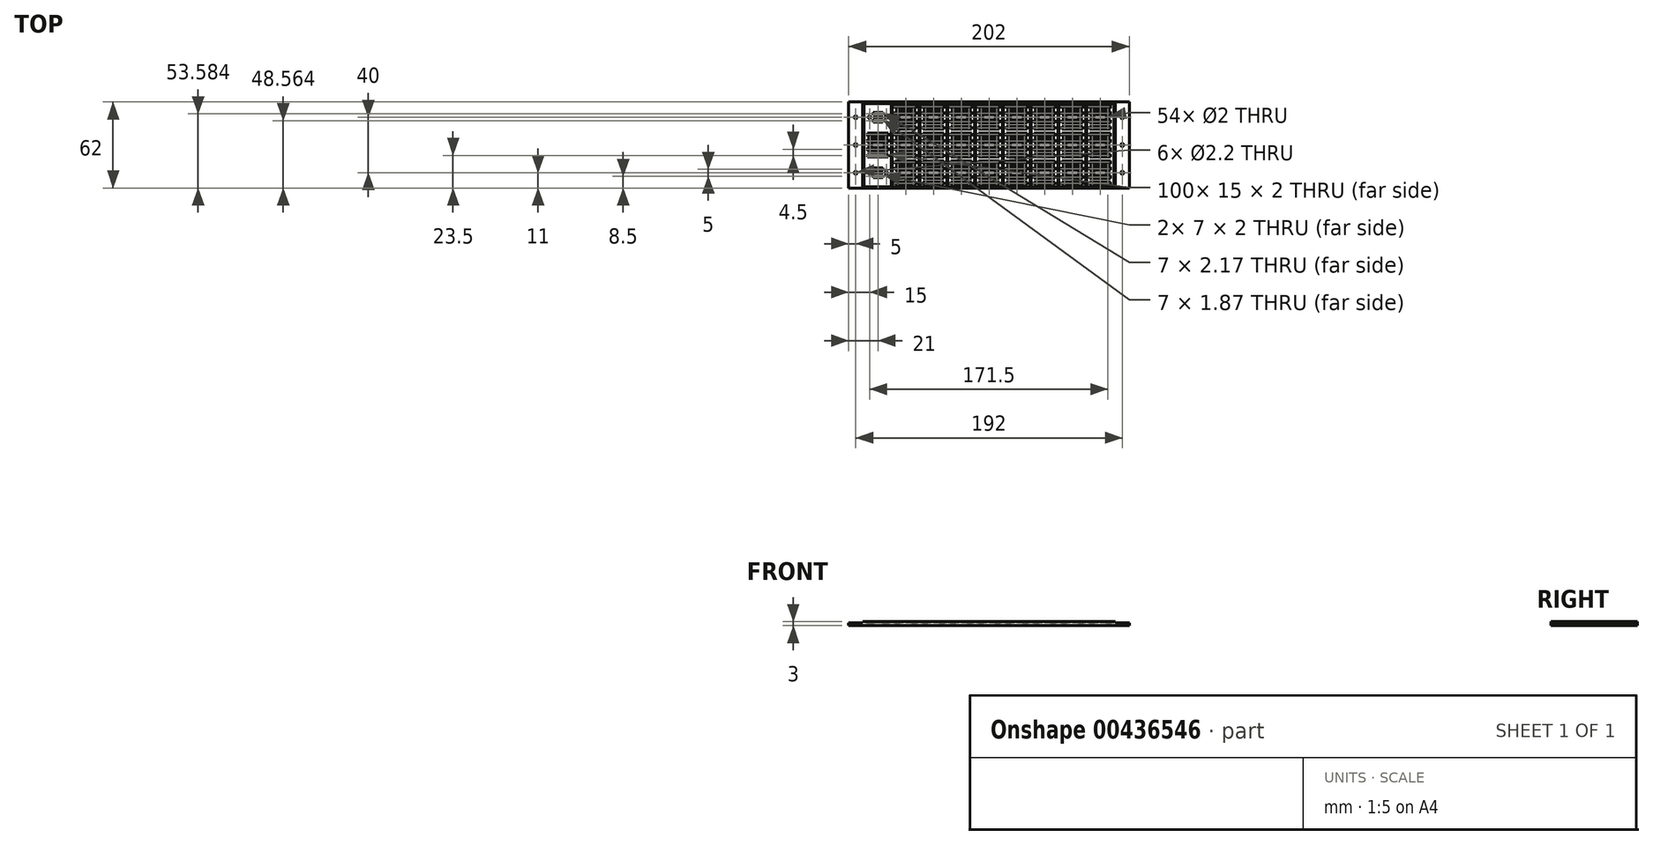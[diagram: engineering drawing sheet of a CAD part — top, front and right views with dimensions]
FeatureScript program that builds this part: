
annotation { "Feature Type Name" : "Feature", "Feature Type Description" : "" }
export const myFeature = defineFeature(function(context is Context, id is Id, definition is map)
    precondition{}
    {
        {
            var Q0;
            Q0=qCreatedBy(makeId("Top.planeOp"),FACE);
            var sketch = newSketch(context, id + "F0", { "sketchPlane" : qUnion([Q0])});
            skLineSegment(sketch, "E0.bottom", {"start": v(91, -31) * mm, "end": v(-91, -31) * mm});
            skLineSegment(sketch, "E0.top", {"start": v(91, 31) * mm, "end": v(-91, 31) * mm});
            skLineSegment(sketch, "E0.left", {"start": v(91, -31) * mm, "end": v(91, 31) * mm});
            skLineSegment(sketch, "E0.right", {"start": v(-91, -31) * mm, "end": v(-91, 31) * mm});
            skPoint(sketch, "E0.middle", {"position": v(0, 0) * mm});
            skSolve(sketch);
        }
        {
            var Q0;
            Q0=qSketchRegion(id+"F0",true);
            extrude(context, id + "F1", {"entities" : qUnion([Q0]), "depth" : 2 * mm});
        }
        {
            var Q0;
            Q0=makeQuery(id+"F1.opExtrude","CAP_FACE",FACE,{"disambiguationData":[OSD([sQuery(id+"F0.wireOp",EDGE,"E0.bottom"),sQuery(id+"F0.wireOp",EDGE,"E0.top"),sQuery(id+"F0.wireOp",EDGE,"E0.left"),sQuery(id+"F0.wireOp",EDGE,"E0.right")])],"isStart":false});
            var sketch = newSketch(context, id + "F2", { "sketchPlane" : qUnion([Q0])});
            skLineSegment(sketch, "E1.bottom", {"start": v(91, -31) * mm, "end": v(-91, -31) * mm});
            skLineSegment(sketch, "E1.top", {"start": v(91, 31) * mm, "end": v(-91, 31) * mm});
            skLineSegment(sketch, "E1.left", {"start": v(91, -31) * mm, "end": v(91, 31) * mm});
            skLineSegment(sketch, "E1.right", {"start": v(-91, -31) * mm, "end": v(-91, 31) * mm});
            skPoint(sketch, "E1.middle", {"position": v(0, 0) * mm});
            skLineSegment(sketch, "E2.bottom", {"start": v(90, -30) * mm, "end": v(-90, -30) * mm});
            skLineSegment(sketch, "E2.top", {"start": v(90, 30) * mm, "end": v(-90, 30) * mm});
            skLineSegment(sketch, "E2.left", {"start": v(90, -30) * mm, "end": v(90, 30) * mm});
            skLineSegment(sketch, "E2.right", {"start": v(-90, -30) * mm, "end": v(-90, 30) * mm});
            skSolve(sketch);
        }
        {
            var Q0;
            Q0=qSketchRegion(id+"F2",true);
            extrude(context, id + "F3", {"entities" : qUnion([Q0]), "operationType" : NewBodyOperationType.ADD, "depth" : 1 * mm});
        }
        {
            var Q0;
            Q0=qCreatedBy(makeId("Top.planeOp"),FACE);
            var sketch = newSketch(context, id + "F4", { "sketchPlane" : qUnion([Q0])});
            skLineSegment(sketch, "E3.bottom", {"start": v(-91, 31) * mm, "end": v(-101, 31) * mm});
            skLineSegment(sketch, "E3.top", {"start": v(-91, -31) * mm, "end": v(-101, -31) * mm});
            skLineSegment(sketch, "E3.left", {"start": v(-91, 31) * mm, "end": v(-91, -31) * mm});
            skLineSegment(sketch, "E3.right", {"start": v(-101, 31) * mm, "end": v(-101, -31) * mm});
            skLineSegment(sketch, "E4.bottom", {"start": v(91, 31) * mm, "end": v(101, 31) * mm});
            skLineSegment(sketch, "E4.top", {"start": v(91, -31) * mm, "end": v(101, -31) * mm});
            skLineSegment(sketch, "E4.left", {"start": v(91, 31) * mm, "end": v(91, -31) * mm});
            skLineSegment(sketch, "E4.right", {"start": v(101, 31) * mm, "end": v(101, -31) * mm});
            skCircle(sketch, "E5", {"center": v(-96, 20) * mm, "radius": 1.1 * mm});
            skPoint(sketch, "E5.centerSnap0", {"position": v(-96, 31) * mm});
            skCircle(sketch, "E6", {"center": v(-96, 0) * mm, "radius": 1.1 * mm});
            skCircle(sketch, "E7", {"center": v(-96, -20) * mm, "radius": 1.1 * mm});
            skCircle(sketch, "E8", {"center": v(96, 20) * mm, "radius": 1.1 * mm});
            skPoint(sketch, "E8.centerSnap0", {"position": v(96, 31) * mm});
            skCircle(sketch, "E9", {"center": v(96, 0) * mm, "radius": 1.1 * mm});
            skPoint(sketch, "E9.centerSnap0", {"position": v(91, 0) * mm});
            skCircle(sketch, "E10", {"center": v(96, -20) * mm, "radius": 1.1 * mm});
            skSolve(sketch);
        }
        {
            var Q0;
            Q0=qSketchRegion(id+"F4",true);
            extrude(context, id + "F5", {"entities" : qUnion([Q0]), "operationType" : NewBodyOperationType.ADD, "depth" : 2 * mm});
        }
        {
            var Q0;
            Q0=makeQuery(id+"F5.boolean.opBoolean","MERGE",FACE,{"derivedFrom":[makeQuery(id+"F1.opExtrude","CAP_FACE",FACE,{"disambiguationData":[OSD([sQuery(id+"F0.wireOp",EDGE,"E0.bottom"),sQuery(id+"F0.wireOp",EDGE,"E0.top"),sQuery(id+"F0.wireOp",EDGE,"E0.left"),sQuery(id+"F0.wireOp",EDGE,"E0.right")])],"isStart":true}),makeQuery(id+"F5.opExtrude","CAP_FACE",FACE,{"disambiguationData":[OSD([sQuery(id+"F4.wireOp",EDGE,"E3.bottom"),sQuery(id+"F4.wireOp",EDGE,"E3.top"),sQuery(id+"F4.wireOp",EDGE,"E3.left"),sQuery(id+"F4.wireOp",EDGE,"E3.right"),sQuery(id+"F4.wireOp",EDGE,"E5"),sQuery(id+"F4.wireOp",EDGE,"E6"),sQuery(id+"F4.wireOp",EDGE,"E7")])],"isStart":true}),makeQuery(id+"F5.opExtrude","CAP_FACE",FACE,{"disambiguationData":[OSD([sQuery(id+"F4.wireOp",EDGE,"E4.bottom"),sQuery(id+"F4.wireOp",EDGE,"E4.top"),sQuery(id+"F4.wireOp",EDGE,"E4.left"),sQuery(id+"F4.wireOp",EDGE,"E4.right"),sQuery(id+"F4.wireOp",EDGE,"E8"),sQuery(id+"F4.wireOp",EDGE,"E9"),sQuery(id+"F4.wireOp",EDGE,"E10")])],"isStart":true})]});
            var sketch = newSketch(context, id + "F6", { "sketchPlane" : qUnion([Q0])});
            skCircle(sketch, "E11", {"center": v(74.5, 20) * mm, "radius": 1 * mm});
            skCircle(sketch, "E12", {"center": v(85.5, 20) * mm, "radius": 1 * mm});
            skLineSegment(sketch, "E13.bottom", {"start": v(87.5, 22) * mm, "end": v(72.5, 22) * mm});
            skLineSegment(sketch, "E13.top", {"start": v(87.5, 24) * mm, "end": v(72.5, 24) * mm});
            skLineSegment(sketch, "E13.left", {"start": v(87.5, 22) * mm, "end": v(87.5, 24) * mm});
            skLineSegment(sketch, "E13.right", {"start": v(72.5, 22) * mm, "end": v(72.5, 24) * mm});
            skPoint(sketch, "E13.middle", {"position": v(80, 23) * mm});
            skLineSegment(sketch, "E14.bottom", {"start": v(87.5, 26.5) * mm, "end": v(72.5, 26.5) * mm});
            skLineSegment(sketch, "E14.top", {"start": v(87.5, 28.5) * mm, "end": v(72.5, 28.5) * mm});
            skLineSegment(sketch, "E14.left", {"start": v(87.5, 26.5) * mm, "end": v(87.5, 28.5) * mm});
            skLineSegment(sketch, "E14.right", {"start": v(72.5, 26.5) * mm, "end": v(72.5, 28.5) * mm});
            skPoint(sketch, "E14.middle", {"position": v(80, 27.5) * mm});
            skLineSegment(sketch, "E15.bottom", {"start": v(87.5, 18) * mm, "end": v(72.5, 18) * mm});
            skLineSegment(sketch, "E15.top", {"start": v(87.5, 16) * mm, "end": v(72.5, 16) * mm});
            skLineSegment(sketch, "E15.left", {"start": v(87.5, 18) * mm, "end": v(87.5, 16) * mm});
            skLineSegment(sketch, "E15.right", {"start": v(72.5, 18) * mm, "end": v(72.5, 16) * mm});
            skPoint(sketch, "E15.middle", {"position": v(80, 17) * mm});
            skLineSegment(sketch, "E16.bottom", {"start": v(87.5, 13.5) * mm, "end": v(72.5, 13.5) * mm});
            skLineSegment(sketch, "E16.top", {"start": v(87.5, 11.5) * mm, "end": v(72.5, 11.5) * mm});
            skLineSegment(sketch, "E16.left", {"start": v(87.5, 13.5) * mm, "end": v(87.5, 11.5) * mm});
            skLineSegment(sketch, "E16.right", {"start": v(72.5, 13.5) * mm, "end": v(72.5, 11.5) * mm});
            skPoint(sketch, "E16.middle", {"position": v(80, 12.5) * mm});
            skLineSegment(sketch, "E17.bottom", {"start": v(89.5, 10.5) * mm, "end": v(70.5, 10.5) * mm, "construction": true});
            skLineSegment(sketch, "E17.top", {"start": v(89.5, 29.5) * mm, "end": v(70.5, 29.5) * mm, "construction": true});
            skLineSegment(sketch, "E17.left", {"start": v(89.5, 10.5) * mm, "end": v(89.5, 29.5) * mm, "construction": true});
            skLineSegment(sketch, "E17.right", {"start": v(70.5, 10.5) * mm, "end": v(70.5, 29.5) * mm, "construction": true});
            skPoint(sketch, "E17.middle", {"position": v(80, 20) * mm});
            skLineSegment(sketch, "E18.0.1.0", {"start": v(87.5, -8.5) * mm, "end": v(72.5, -8.5) * mm});
            skLineSegment(sketch, "E18.0.1.1", {"start": v(87.5, 8.5) * mm, "end": v(72.5, 8.5) * mm});
            skLineSegment(sketch, "E18.0.1.2", {"start": v(87.5, -4) * mm, "end": v(72.5, -4) * mm});
            skLineSegment(sketch, "E18.0.1.3", {"start": v(89.5, -9.5) * mm, "end": v(70.5, -9.5) * mm, "construction": true});
            skPoint(sketch, "E18.0.1.4", {"position": v(80, -3) * mm});
            skLineSegment(sketch, "E18.0.1.5", {"start": v(89.5, 9.5) * mm, "end": v(70.5, 9.5) * mm, "construction": true});
            skLineSegment(sketch, "E18.0.1.6", {"start": v(87.5, 6.5) * mm, "end": v(72.5, 6.5) * mm});
            skLineSegment(sketch, "E18.0.1.7", {"start": v(89.5, -9.5) * mm, "end": v(89.5, 9.5) * mm, "construction": true});
            skPoint(sketch, "E18.0.1.8", {"position": v(80, 3) * mm});
            skLineSegment(sketch, "E18.0.1.9", {"start": v(87.5, -6.5) * mm, "end": v(72.5, -6.5) * mm});
            skLineSegment(sketch, "E18.0.1.10", {"start": v(87.5, 4) * mm, "end": v(72.5, 4) * mm});
            skLineSegment(sketch, "E18.0.1.11", {"start": v(87.5, -2) * mm, "end": v(72.5, -2) * mm});
            skPoint(sketch, "E18.0.1.12", {"position": v(80, 7.5) * mm});
            skLineSegment(sketch, "E18.0.1.13", {"start": v(70.5, -9.5) * mm, "end": v(70.5, 9.5) * mm, "construction": true});
            skPoint(sketch, "E18.0.1.14", {"position": v(80, -7.5) * mm});
            skLineSegment(sketch, "E18.0.1.15", {"start": v(87.5, 2) * mm, "end": v(72.5, 2) * mm});
            skCircle(sketch, "E18.0.1.16", {"center": v(74.5, 0) * mm, "radius": 1 * mm});
            skCircle(sketch, "E18.0.1.17", {"center": v(85.5, 0) * mm, "radius": 1 * mm});
            skPoint(sketch, "E18.0.1.18", {"position": v(80, 0) * mm});
            skLineSegment(sketch, "E18.0.1.19", {"start": v(72.5, -6.5) * mm, "end": v(72.5, -8.5) * mm});
            skLineSegment(sketch, "E18.0.1.20", {"start": v(87.5, 6.5) * mm, "end": v(87.5, 8.5) * mm});
            skLineSegment(sketch, "E18.0.1.21", {"start": v(72.5, 6.5) * mm, "end": v(72.5, 8.5) * mm});
            skLineSegment(sketch, "E18.0.1.22", {"start": v(87.5, -2) * mm, "end": v(87.5, -4) * mm});
            skLineSegment(sketch, "E18.0.1.23", {"start": v(87.5, 2) * mm, "end": v(87.5, 4) * mm});
            skLineSegment(sketch, "E18.0.1.24", {"start": v(72.5, 2) * mm, "end": v(72.5, 4) * mm});
            skLineSegment(sketch, "E18.0.1.25", {"start": v(87.5, -6.5) * mm, "end": v(87.5, -8.5) * mm});
            skLineSegment(sketch, "E18.0.1.26", {"start": v(72.5, -2) * mm, "end": v(72.5, -4) * mm});
            skLineSegment(sketch, "E18.0.2.0", {"start": v(87.5, -28.5) * mm, "end": v(72.5, -28.5) * mm});
            skLineSegment(sketch, "E18.0.2.1", {"start": v(87.5, -11.5) * mm, "end": v(72.5, -11.5) * mm});
            skLineSegment(sketch, "E18.0.2.2", {"start": v(87.5, -24) * mm, "end": v(72.5, -24) * mm});
            skLineSegment(sketch, "E18.0.2.3", {"start": v(89.5, -29.5) * mm, "end": v(70.5, -29.5) * mm, "construction": true});
            skPoint(sketch, "E18.0.2.4", {"position": v(80, -23) * mm});
            skLineSegment(sketch, "E18.0.2.5", {"start": v(89.5, -10.5) * mm, "end": v(70.5, -10.5) * mm, "construction": true});
            skLineSegment(sketch, "E18.0.2.6", {"start": v(87.5, -13.5) * mm, "end": v(72.5, -13.5) * mm});
            skLineSegment(sketch, "E18.0.2.7", {"start": v(89.5, -29.5) * mm, "end": v(89.5, -10.5) * mm, "construction": true});
            skPoint(sketch, "E18.0.2.8", {"position": v(80, -17) * mm});
            skLineSegment(sketch, "E18.0.2.9", {"start": v(87.5, -26.5) * mm, "end": v(72.5, -26.5) * mm});
            skLineSegment(sketch, "E18.0.2.10", {"start": v(87.5, -16) * mm, "end": v(72.5, -16) * mm});
            skLineSegment(sketch, "E18.0.2.11", {"start": v(87.5, -22) * mm, "end": v(72.5, -22) * mm});
            skPoint(sketch, "E18.0.2.12", {"position": v(80, -12.5) * mm});
            skLineSegment(sketch, "E18.0.2.13", {"start": v(70.5, -29.5) * mm, "end": v(70.5, -10.5) * mm, "construction": true});
            skPoint(sketch, "E18.0.2.14", {"position": v(80, -27.5) * mm});
            skLineSegment(sketch, "E18.0.2.15", {"start": v(87.5, -18) * mm, "end": v(72.5, -18) * mm});
            skCircle(sketch, "E18.0.2.16", {"center": v(74.5, -20) * mm, "radius": 1 * mm});
            skCircle(sketch, "E18.0.2.17", {"center": v(85.5, -20) * mm, "radius": 1 * mm});
            skPoint(sketch, "E18.0.2.18", {"position": v(80, -20) * mm});
            skLineSegment(sketch, "E18.0.2.19", {"start": v(72.5, -26.5) * mm, "end": v(72.5, -28.5) * mm});
            skLineSegment(sketch, "E18.0.2.20", {"start": v(87.5, -13.5) * mm, "end": v(87.5, -11.5) * mm});
            skLineSegment(sketch, "E18.0.2.21", {"start": v(72.5, -13.5) * mm, "end": v(72.5, -11.5) * mm});
            skLineSegment(sketch, "E18.0.2.22", {"start": v(87.5, -22) * mm, "end": v(87.5, -24) * mm});
            skLineSegment(sketch, "E18.0.2.23", {"start": v(87.5, -18) * mm, "end": v(87.5, -16) * mm});
            skLineSegment(sketch, "E18.0.2.24", {"start": v(72.5, -18) * mm, "end": v(72.5, -16) * mm});
            skLineSegment(sketch, "E18.0.2.25", {"start": v(87.5, -26.5) * mm, "end": v(87.5, -28.5) * mm});
            skLineSegment(sketch, "E18.0.2.26", {"start": v(72.5, -22) * mm, "end": v(72.5, -24) * mm});
            skLineSegment(sketch, "E18.1.0.0", {"start": v(67.5, 11.5) * mm, "end": v(52.5, 11.5) * mm});
            skLineSegment(sketch, "E18.1.0.1", {"start": v(67.5, 28.5) * mm, "end": v(52.5, 28.5) * mm});
            skLineSegment(sketch, "E18.1.0.2", {"start": v(67.5, 16) * mm, "end": v(52.5, 16) * mm});
            skLineSegment(sketch, "E18.1.0.3", {"start": v(69.5, 10.5) * mm, "end": v(50.5, 10.5) * mm, "construction": true});
            skPoint(sketch, "E18.1.0.4", {"position": v(60, 17) * mm});
            skLineSegment(sketch, "E18.1.0.5", {"start": v(69.5, 29.5) * mm, "end": v(50.5, 29.5) * mm, "construction": true});
            skLineSegment(sketch, "E18.1.0.6", {"start": v(67.5, 26.5) * mm, "end": v(52.5, 26.5) * mm});
            skLineSegment(sketch, "E18.1.0.7", {"start": v(69.5, 10.5) * mm, "end": v(69.5, 29.5) * mm, "construction": true});
            skPoint(sketch, "E18.1.0.8", {"position": v(60, 23) * mm});
            skLineSegment(sketch, "E18.1.0.9", {"start": v(67.5, 13.5) * mm, "end": v(52.5, 13.5) * mm});
            skLineSegment(sketch, "E18.1.0.10", {"start": v(67.5, 24) * mm, "end": v(52.5, 24) * mm});
            skLineSegment(sketch, "E18.1.0.11", {"start": v(67.5, 18) * mm, "end": v(52.5, 18) * mm});
            skPoint(sketch, "E18.1.0.12", {"position": v(60, 27.5) * mm});
            skLineSegment(sketch, "E18.1.0.13", {"start": v(50.5, 10.5) * mm, "end": v(50.5, 29.5) * mm, "construction": true});
            skPoint(sketch, "E18.1.0.14", {"position": v(60, 12.5) * mm});
            skLineSegment(sketch, "E18.1.0.15", {"start": v(67.5, 22) * mm, "end": v(52.5, 22) * mm});
            skCircle(sketch, "E18.1.0.16", {"center": v(54.5, 20) * mm, "radius": 1 * mm});
            skCircle(sketch, "E18.1.0.17", {"center": v(65.5, 20) * mm, "radius": 1 * mm});
            skPoint(sketch, "E18.1.0.18", {"position": v(60, 20) * mm});
            skLineSegment(sketch, "E18.1.0.19", {"start": v(52.5, 13.5) * mm, "end": v(52.5, 11.5) * mm});
            skLineSegment(sketch, "E18.1.0.20", {"start": v(67.5, 26.5) * mm, "end": v(67.5, 28.5) * mm});
            skLineSegment(sketch, "E18.1.0.21", {"start": v(52.5, 26.5) * mm, "end": v(52.5, 28.5) * mm});
            skLineSegment(sketch, "E18.1.0.22", {"start": v(67.5, 18) * mm, "end": v(67.5, 16) * mm});
            skLineSegment(sketch, "E18.1.0.23", {"start": v(67.5, 22) * mm, "end": v(67.5, 24) * mm});
            skLineSegment(sketch, "E18.1.0.24", {"start": v(52.5, 22) * mm, "end": v(52.5, 24) * mm});
            skLineSegment(sketch, "E18.1.0.25", {"start": v(67.5, 13.5) * mm, "end": v(67.5, 11.5) * mm});
            skLineSegment(sketch, "E18.1.0.26", {"start": v(52.5, 18) * mm, "end": v(52.5, 16) * mm});
            skLineSegment(sketch, "E18.1.1.0", {"start": v(67.5, -8.5) * mm, "end": v(52.5, -8.5) * mm});
            skLineSegment(sketch, "E18.1.1.1", {"start": v(67.5, 8.5) * mm, "end": v(52.5, 8.5) * mm});
            skLineSegment(sketch, "E18.1.1.2", {"start": v(67.5, -4) * mm, "end": v(52.5, -4) * mm});
            skLineSegment(sketch, "E18.1.1.3", {"start": v(69.5, -9.5) * mm, "end": v(50.5, -9.5) * mm, "construction": true});
            skPoint(sketch, "E18.1.1.4", {"position": v(60, -3) * mm});
            skLineSegment(sketch, "E18.1.1.5", {"start": v(69.5, 9.5) * mm, "end": v(50.5, 9.5) * mm, "construction": true});
            skLineSegment(sketch, "E18.1.1.6", {"start": v(67.5, 6.5) * mm, "end": v(52.5, 6.5) * mm});
            skLineSegment(sketch, "E18.1.1.7", {"start": v(69.5, -9.5) * mm, "end": v(69.5, 9.5) * mm, "construction": true});
            skPoint(sketch, "E18.1.1.8", {"position": v(60, 3) * mm});
            skLineSegment(sketch, "E18.1.1.9", {"start": v(67.5, -6.5) * mm, "end": v(52.5, -6.5) * mm});
            skLineSegment(sketch, "E18.1.1.10", {"start": v(67.5, 4) * mm, "end": v(52.5, 4) * mm});
            skLineSegment(sketch, "E18.1.1.11", {"start": v(67.5, -2) * mm, "end": v(52.5, -2) * mm});
            skPoint(sketch, "E18.1.1.12", {"position": v(60, 7.5) * mm});
            skLineSegment(sketch, "E18.1.1.13", {"start": v(50.5, -9.5) * mm, "end": v(50.5, 9.5) * mm, "construction": true});
            skPoint(sketch, "E18.1.1.14", {"position": v(60, -7.5) * mm});
            skLineSegment(sketch, "E18.1.1.15", {"start": v(67.5, 2) * mm, "end": v(52.5, 2) * mm});
            skCircle(sketch, "E18.1.1.16", {"center": v(54.5, 0) * mm, "radius": 1 * mm});
            skCircle(sketch, "E18.1.1.17", {"center": v(65.5, 0) * mm, "radius": 1 * mm});
            skPoint(sketch, "E18.1.1.18", {"position": v(60, 0) * mm});
            skLineSegment(sketch, "E18.1.1.19", {"start": v(52.5, -6.5) * mm, "end": v(52.5, -8.5) * mm});
            skLineSegment(sketch, "E18.1.1.20", {"start": v(67.5, 6.5) * mm, "end": v(67.5, 8.5) * mm});
            skLineSegment(sketch, "E18.1.1.21", {"start": v(52.5, 6.5) * mm, "end": v(52.5, 8.5) * mm});
            skLineSegment(sketch, "E18.1.1.22", {"start": v(67.5, -2) * mm, "end": v(67.5, -4) * mm});
            skLineSegment(sketch, "E18.1.1.23", {"start": v(67.5, 2) * mm, "end": v(67.5, 4) * mm});
            skLineSegment(sketch, "E18.1.1.24", {"start": v(52.5, 2) * mm, "end": v(52.5, 4) * mm});
            skLineSegment(sketch, "E18.1.1.25", {"start": v(67.5, -6.5) * mm, "end": v(67.5, -8.5) * mm});
            skLineSegment(sketch, "E18.1.1.26", {"start": v(52.5, -2) * mm, "end": v(52.5, -4) * mm});
            skLineSegment(sketch, "E18.1.2.0", {"start": v(67.5, -28.5) * mm, "end": v(52.5, -28.5) * mm});
            skLineSegment(sketch, "E18.1.2.1", {"start": v(67.5, -11.5) * mm, "end": v(52.5, -11.5) * mm});
            skLineSegment(sketch, "E18.1.2.2", {"start": v(67.5, -24) * mm, "end": v(52.5, -24) * mm});
            skLineSegment(sketch, "E18.1.2.3", {"start": v(69.5, -29.5) * mm, "end": v(50.5, -29.5) * mm, "construction": true});
            skPoint(sketch, "E18.1.2.4", {"position": v(60, -23) * mm});
            skLineSegment(sketch, "E18.1.2.5", {"start": v(69.5, -10.5) * mm, "end": v(50.5, -10.5) * mm, "construction": true});
            skLineSegment(sketch, "E18.1.2.6", {"start": v(67.5, -13.5) * mm, "end": v(52.5, -13.5) * mm});
            skLineSegment(sketch, "E18.1.2.7", {"start": v(69.5, -29.5) * mm, "end": v(69.5, -10.5) * mm, "construction": true});
            skPoint(sketch, "E18.1.2.8", {"position": v(60, -17) * mm});
            skLineSegment(sketch, "E18.1.2.9", {"start": v(67.5, -26.5) * mm, "end": v(52.5, -26.5) * mm});
            skLineSegment(sketch, "E18.1.2.10", {"start": v(67.5, -16) * mm, "end": v(52.5, -16) * mm});
            skLineSegment(sketch, "E18.1.2.11", {"start": v(67.5, -22) * mm, "end": v(52.5, -22) * mm});
            skPoint(sketch, "E18.1.2.12", {"position": v(60, -12.5) * mm});
            skLineSegment(sketch, "E18.1.2.13", {"start": v(50.5, -29.5) * mm, "end": v(50.5, -10.5) * mm, "construction": true});
            skPoint(sketch, "E18.1.2.14", {"position": v(60, -27.5) * mm});
            skLineSegment(sketch, "E18.1.2.15", {"start": v(67.5, -18) * mm, "end": v(52.5, -18) * mm});
            skCircle(sketch, "E18.1.2.16", {"center": v(54.5, -20) * mm, "radius": 1 * mm});
            skCircle(sketch, "E18.1.2.17", {"center": v(65.5, -20) * mm, "radius": 1 * mm});
            skPoint(sketch, "E18.1.2.18", {"position": v(60, -20) * mm});
            skLineSegment(sketch, "E18.1.2.19", {"start": v(52.5, -26.5) * mm, "end": v(52.5, -28.5) * mm});
            skLineSegment(sketch, "E18.1.2.20", {"start": v(67.5, -13.5) * mm, "end": v(67.5, -11.5) * mm});
            skLineSegment(sketch, "E18.1.2.21", {"start": v(52.5, -13.5) * mm, "end": v(52.5, -11.5) * mm});
            skLineSegment(sketch, "E18.1.2.22", {"start": v(67.5, -22) * mm, "end": v(67.5, -24) * mm});
            skLineSegment(sketch, "E18.1.2.23", {"start": v(67.5, -18) * mm, "end": v(67.5, -16) * mm});
            skLineSegment(sketch, "E18.1.2.24", {"start": v(52.5, -18) * mm, "end": v(52.5, -16) * mm});
            skLineSegment(sketch, "E18.1.2.25", {"start": v(67.5, -26.5) * mm, "end": v(67.5, -28.5) * mm});
            skLineSegment(sketch, "E18.1.2.26", {"start": v(52.5, -22) * mm, "end": v(52.5, -24) * mm});
            skLineSegment(sketch, "E18.2.0.0", {"start": v(47.5, 11.5) * mm, "end": v(32.5, 11.5) * mm});
            skLineSegment(sketch, "E18.2.0.1", {"start": v(47.5, 28.5) * mm, "end": v(32.5, 28.5) * mm});
            skLineSegment(sketch, "E18.2.0.2", {"start": v(47.5, 16) * mm, "end": v(32.5, 16) * mm});
            skLineSegment(sketch, "E18.2.0.3", {"start": v(49.5, 10.5) * mm, "end": v(30.5, 10.5) * mm, "construction": true});
            skPoint(sketch, "E18.2.0.4", {"position": v(40, 17) * mm});
            skLineSegment(sketch, "E18.2.0.5", {"start": v(49.5, 29.5) * mm, "end": v(30.5, 29.5) * mm, "construction": true});
            skLineSegment(sketch, "E18.2.0.6", {"start": v(47.5, 26.5) * mm, "end": v(32.5, 26.5) * mm});
            skLineSegment(sketch, "E18.2.0.7", {"start": v(49.5, 10.5) * mm, "end": v(49.5, 29.5) * mm, "construction": true});
            skPoint(sketch, "E18.2.0.8", {"position": v(40, 23) * mm});
            skLineSegment(sketch, "E18.2.0.9", {"start": v(47.5, 13.5) * mm, "end": v(32.5, 13.5) * mm});
            skLineSegment(sketch, "E18.2.0.10", {"start": v(47.5, 24) * mm, "end": v(32.5, 24) * mm});
            skLineSegment(sketch, "E18.2.0.11", {"start": v(47.5, 18) * mm, "end": v(32.5, 18) * mm});
            skPoint(sketch, "E18.2.0.12", {"position": v(40, 27.5) * mm});
            skLineSegment(sketch, "E18.2.0.13", {"start": v(30.5, 10.5) * mm, "end": v(30.5, 29.5) * mm, "construction": true});
            skPoint(sketch, "E18.2.0.14", {"position": v(40, 12.5) * mm});
            skLineSegment(sketch, "E18.2.0.15", {"start": v(47.5, 22) * mm, "end": v(32.5, 22) * mm});
            skCircle(sketch, "E18.2.0.16", {"center": v(34.5, 20) * mm, "radius": 1 * mm});
            skCircle(sketch, "E18.2.0.17", {"center": v(45.5, 20) * mm, "radius": 1 * mm});
            skPoint(sketch, "E18.2.0.18", {"position": v(40, 20) * mm});
            skLineSegment(sketch, "E18.2.0.19", {"start": v(32.5, 13.5) * mm, "end": v(32.5, 11.5) * mm});
            skLineSegment(sketch, "E18.2.0.20", {"start": v(47.5, 26.5) * mm, "end": v(47.5, 28.5) * mm});
            skLineSegment(sketch, "E18.2.0.21", {"start": v(32.5, 26.5) * mm, "end": v(32.5, 28.5) * mm});
            skLineSegment(sketch, "E18.2.0.22", {"start": v(47.5, 18) * mm, "end": v(47.5, 16) * mm});
            skLineSegment(sketch, "E18.2.0.23", {"start": v(47.5, 22) * mm, "end": v(47.5, 24) * mm});
            skLineSegment(sketch, "E18.2.0.24", {"start": v(32.5, 22) * mm, "end": v(32.5, 24) * mm});
            skLineSegment(sketch, "E18.2.0.25", {"start": v(47.5, 13.5) * mm, "end": v(47.5, 11.5) * mm});
            skLineSegment(sketch, "E18.2.0.26", {"start": v(32.5, 18) * mm, "end": v(32.5, 16) * mm});
            skLineSegment(sketch, "E18.2.1.0", {"start": v(47.5, -8.5) * mm, "end": v(32.5, -8.5) * mm});
            skLineSegment(sketch, "E18.2.1.1", {"start": v(47.5, 8.5) * mm, "end": v(32.5, 8.5) * mm});
            skLineSegment(sketch, "E18.2.1.2", {"start": v(47.5, -4) * mm, "end": v(32.5, -4) * mm});
            skLineSegment(sketch, "E18.2.1.3", {"start": v(49.5, -9.5) * mm, "end": v(30.5, -9.5) * mm, "construction": true});
            skPoint(sketch, "E18.2.1.4", {"position": v(40, -3) * mm});
            skLineSegment(sketch, "E18.2.1.5", {"start": v(49.5, 9.5) * mm, "end": v(30.5, 9.5) * mm, "construction": true});
            skLineSegment(sketch, "E18.2.1.6", {"start": v(47.5, 6.5) * mm, "end": v(32.5, 6.5) * mm});
            skLineSegment(sketch, "E18.2.1.7", {"start": v(49.5, -9.5) * mm, "end": v(49.5, 9.5) * mm, "construction": true});
            skPoint(sketch, "E18.2.1.8", {"position": v(40, 3) * mm});
            skLineSegment(sketch, "E18.2.1.9", {"start": v(47.5, -6.5) * mm, "end": v(32.5, -6.5) * mm});
            skLineSegment(sketch, "E18.2.1.10", {"start": v(47.5, 4) * mm, "end": v(32.5, 4) * mm});
            skLineSegment(sketch, "E18.2.1.11", {"start": v(47.5, -2) * mm, "end": v(32.5, -2) * mm});
            skPoint(sketch, "E18.2.1.12", {"position": v(40, 7.5) * mm});
            skLineSegment(sketch, "E18.2.1.13", {"start": v(30.5, -9.5) * mm, "end": v(30.5, 9.5) * mm, "construction": true});
            skPoint(sketch, "E18.2.1.14", {"position": v(40, -7.5) * mm});
            skLineSegment(sketch, "E18.2.1.15", {"start": v(47.5, 2) * mm, "end": v(32.5, 2) * mm});
            skCircle(sketch, "E18.2.1.16", {"center": v(34.5, 0) * mm, "radius": 1 * mm});
            skCircle(sketch, "E18.2.1.17", {"center": v(45.5, 0) * mm, "radius": 1 * mm});
            skPoint(sketch, "E18.2.1.18", {"position": v(40, 0) * mm});
            skLineSegment(sketch, "E18.2.1.19", {"start": v(32.5, -6.5) * mm, "end": v(32.5, -8.5) * mm});
            skLineSegment(sketch, "E18.2.1.20", {"start": v(47.5, 6.5) * mm, "end": v(47.5, 8.5) * mm});
            skLineSegment(sketch, "E18.2.1.21", {"start": v(32.5, 6.5) * mm, "end": v(32.5, 8.5) * mm});
            skLineSegment(sketch, "E18.2.1.22", {"start": v(47.5, -2) * mm, "end": v(47.5, -4) * mm});
            skLineSegment(sketch, "E18.2.1.23", {"start": v(47.5, 2) * mm, "end": v(47.5, 4) * mm});
            skLineSegment(sketch, "E18.2.1.24", {"start": v(32.5, 2) * mm, "end": v(32.5, 4) * mm});
            skLineSegment(sketch, "E18.2.1.25", {"start": v(47.5, -6.5) * mm, "end": v(47.5, -8.5) * mm});
            skLineSegment(sketch, "E18.2.1.26", {"start": v(32.5, -2) * mm, "end": v(32.5, -4) * mm});
            skLineSegment(sketch, "E18.2.2.0", {"start": v(47.5, -28.5) * mm, "end": v(32.5, -28.5) * mm});
            skLineSegment(sketch, "E18.2.2.1", {"start": v(47.5, -11.5) * mm, "end": v(32.5, -11.5) * mm});
            skLineSegment(sketch, "E18.2.2.2", {"start": v(47.5, -24) * mm, "end": v(32.5, -24) * mm});
            skLineSegment(sketch, "E18.2.2.3", {"start": v(49.5, -29.5) * mm, "end": v(30.5, -29.5) * mm, "construction": true});
            skPoint(sketch, "E18.2.2.4", {"position": v(40, -23) * mm});
            skLineSegment(sketch, "E18.2.2.5", {"start": v(49.5, -10.5) * mm, "end": v(30.5, -10.5) * mm, "construction": true});
            skLineSegment(sketch, "E18.2.2.6", {"start": v(47.5, -13.5) * mm, "end": v(32.5, -13.5) * mm});
            skLineSegment(sketch, "E18.2.2.7", {"start": v(49.5, -29.5) * mm, "end": v(49.5, -10.5) * mm, "construction": true});
            skPoint(sketch, "E18.2.2.8", {"position": v(40, -17) * mm});
            skLineSegment(sketch, "E18.2.2.9", {"start": v(47.5, -26.5) * mm, "end": v(32.5, -26.5) * mm});
            skLineSegment(sketch, "E18.2.2.10", {"start": v(47.5, -16) * mm, "end": v(32.5, -16) * mm});
            skLineSegment(sketch, "E18.2.2.11", {"start": v(47.5, -22) * mm, "end": v(32.5, -22) * mm});
            skPoint(sketch, "E18.2.2.12", {"position": v(40, -12.5) * mm});
            skLineSegment(sketch, "E18.2.2.13", {"start": v(30.5, -29.5) * mm, "end": v(30.5, -10.5) * mm, "construction": true});
            skPoint(sketch, "E18.2.2.14", {"position": v(40, -27.5) * mm});
            skLineSegment(sketch, "E18.2.2.15", {"start": v(47.5, -18) * mm, "end": v(32.5, -18) * mm});
            skCircle(sketch, "E18.2.2.16", {"center": v(34.5, -20) * mm, "radius": 1 * mm});
            skCircle(sketch, "E18.2.2.17", {"center": v(45.5, -20) * mm, "radius": 1 * mm});
            skPoint(sketch, "E18.2.2.18", {"position": v(40, -20) * mm});
            skLineSegment(sketch, "E18.2.2.19", {"start": v(32.5, -26.5) * mm, "end": v(32.5, -28.5) * mm});
            skLineSegment(sketch, "E18.2.2.20", {"start": v(47.5, -13.5) * mm, "end": v(47.5, -11.5) * mm});
            skLineSegment(sketch, "E18.2.2.21", {"start": v(32.5, -13.5) * mm, "end": v(32.5, -11.5) * mm});
            skLineSegment(sketch, "E18.2.2.22", {"start": v(47.5, -22) * mm, "end": v(47.5, -24) * mm});
            skLineSegment(sketch, "E18.2.2.23", {"start": v(47.5, -18) * mm, "end": v(47.5, -16) * mm});
            skLineSegment(sketch, "E18.2.2.24", {"start": v(32.5, -18) * mm, "end": v(32.5, -16) * mm});
            skLineSegment(sketch, "E18.2.2.25", {"start": v(47.5, -26.5) * mm, "end": v(47.5, -28.5) * mm});
            skLineSegment(sketch, "E18.2.2.26", {"start": v(32.5, -22) * mm, "end": v(32.5, -24) * mm});
            skLineSegment(sketch, "E18.3.0.0", {"start": v(27.5, 11.5) * mm, "end": v(12.5, 11.5) * mm});
            skLineSegment(sketch, "E18.3.0.1", {"start": v(27.5, 28.5) * mm, "end": v(12.5, 28.5) * mm});
            skLineSegment(sketch, "E18.3.0.2", {"start": v(27.5, 16) * mm, "end": v(12.5, 16) * mm});
            skLineSegment(sketch, "E18.3.0.3", {"start": v(29.5, 10.5) * mm, "end": v(10.5, 10.5) * mm, "construction": true});
            skPoint(sketch, "E18.3.0.4", {"position": v(20, 17) * mm});
            skLineSegment(sketch, "E18.3.0.5", {"start": v(29.5, 29.5) * mm, "end": v(10.5, 29.5) * mm, "construction": true});
            skLineSegment(sketch, "E18.3.0.6", {"start": v(27.5, 26.5) * mm, "end": v(12.5, 26.5) * mm});
            skLineSegment(sketch, "E18.3.0.7", {"start": v(29.5, 10.5) * mm, "end": v(29.5, 29.5) * mm, "construction": true});
            skPoint(sketch, "E18.3.0.8", {"position": v(20, 23) * mm});
            skLineSegment(sketch, "E18.3.0.9", {"start": v(27.5, 13.5) * mm, "end": v(12.5, 13.5) * mm});
            skLineSegment(sketch, "E18.3.0.10", {"start": v(27.5, 24) * mm, "end": v(12.5, 24) * mm});
            skLineSegment(sketch, "E18.3.0.11", {"start": v(27.5, 18) * mm, "end": v(12.5, 18) * mm});
            skPoint(sketch, "E18.3.0.12", {"position": v(20, 27.5) * mm});
            skLineSegment(sketch, "E18.3.0.13", {"start": v(10.5, 10.5) * mm, "end": v(10.5, 29.5) * mm, "construction": true});
            skPoint(sketch, "E18.3.0.14", {"position": v(20, 12.5) * mm});
            skLineSegment(sketch, "E18.3.0.15", {"start": v(27.5, 22) * mm, "end": v(12.5, 22) * mm});
            skCircle(sketch, "E18.3.0.16", {"center": v(14.5, 20) * mm, "radius": 1 * mm});
            skCircle(sketch, "E18.3.0.17", {"center": v(25.5, 20) * mm, "radius": 1 * mm});
            skPoint(sketch, "E18.3.0.18", {"position": v(20, 20) * mm});
            skLineSegment(sketch, "E18.3.0.19", {"start": v(12.5, 13.5) * mm, "end": v(12.5, 11.5) * mm});
            skLineSegment(sketch, "E18.3.0.20", {"start": v(27.5, 26.5) * mm, "end": v(27.5, 28.5) * mm});
            skLineSegment(sketch, "E18.3.0.21", {"start": v(12.5, 26.5) * mm, "end": v(12.5, 28.5) * mm});
            skLineSegment(sketch, "E18.3.0.22", {"start": v(27.5, 18) * mm, "end": v(27.5, 16) * mm});
            skLineSegment(sketch, "E18.3.0.23", {"start": v(27.5, 22) * mm, "end": v(27.5, 24) * mm});
            skLineSegment(sketch, "E18.3.0.24", {"start": v(12.5, 22) * mm, "end": v(12.5, 24) * mm});
            skLineSegment(sketch, "E18.3.0.25", {"start": v(27.5, 13.5) * mm, "end": v(27.5, 11.5) * mm});
            skLineSegment(sketch, "E18.3.0.26", {"start": v(12.5, 18) * mm, "end": v(12.5, 16) * mm});
            skLineSegment(sketch, "E18.3.1.0", {"start": v(27.5, -8.5) * mm, "end": v(12.5, -8.5) * mm});
            skLineSegment(sketch, "E18.3.1.1", {"start": v(27.5, 8.5) * mm, "end": v(12.5, 8.5) * mm});
            skLineSegment(sketch, "E18.3.1.2", {"start": v(27.5, -4) * mm, "end": v(12.5, -4) * mm});
            skLineSegment(sketch, "E18.3.1.3", {"start": v(29.5, -9.5) * mm, "end": v(10.5, -9.5) * mm, "construction": true});
            skPoint(sketch, "E18.3.1.4", {"position": v(20, -3) * mm});
            skLineSegment(sketch, "E18.3.1.5", {"start": v(29.5, 9.5) * mm, "end": v(10.5, 9.5) * mm, "construction": true});
            skLineSegment(sketch, "E18.3.1.6", {"start": v(27.5, 6.5) * mm, "end": v(12.5, 6.5) * mm});
            skLineSegment(sketch, "E18.3.1.7", {"start": v(29.5, -9.5) * mm, "end": v(29.5, 9.5) * mm, "construction": true});
            skPoint(sketch, "E18.3.1.8", {"position": v(20, 3) * mm});
            skLineSegment(sketch, "E18.3.1.9", {"start": v(27.5, -6.5) * mm, "end": v(12.5, -6.5) * mm});
            skLineSegment(sketch, "E18.3.1.10", {"start": v(27.5, 4) * mm, "end": v(12.5, 4) * mm});
            skLineSegment(sketch, "E18.3.1.11", {"start": v(27.5, -2) * mm, "end": v(12.5, -2) * mm});
            skPoint(sketch, "E18.3.1.12", {"position": v(20, 7.5) * mm});
            skLineSegment(sketch, "E18.3.1.13", {"start": v(10.5, -9.5) * mm, "end": v(10.5, 9.5) * mm, "construction": true});
            skPoint(sketch, "E18.3.1.14", {"position": v(20, -7.5) * mm});
            skLineSegment(sketch, "E18.3.1.15", {"start": v(27.5, 2) * mm, "end": v(12.5, 2) * mm});
            skCircle(sketch, "E18.3.1.16", {"center": v(14.5, 0) * mm, "radius": 1 * mm});
            skCircle(sketch, "E18.3.1.17", {"center": v(25.5, 0) * mm, "radius": 1 * mm});
            skPoint(sketch, "E18.3.1.18", {"position": v(20, 0) * mm});
            skLineSegment(sketch, "E18.3.1.19", {"start": v(12.5, -6.5) * mm, "end": v(12.5, -8.5) * mm});
            skLineSegment(sketch, "E18.3.1.20", {"start": v(27.5, 6.5) * mm, "end": v(27.5, 8.5) * mm});
            skLineSegment(sketch, "E18.3.1.21", {"start": v(12.5, 6.5) * mm, "end": v(12.5, 8.5) * mm});
            skLineSegment(sketch, "E18.3.1.22", {"start": v(27.5, -2) * mm, "end": v(27.5, -4) * mm});
            skLineSegment(sketch, "E18.3.1.23", {"start": v(27.5, 2) * mm, "end": v(27.5, 4) * mm});
            skLineSegment(sketch, "E18.3.1.24", {"start": v(12.5, 2) * mm, "end": v(12.5, 4) * mm});
            skLineSegment(sketch, "E18.3.1.25", {"start": v(27.5, -6.5) * mm, "end": v(27.5, -8.5) * mm});
            skLineSegment(sketch, "E18.3.1.26", {"start": v(12.5, -2) * mm, "end": v(12.5, -4) * mm});
            skLineSegment(sketch, "E18.3.2.0", {"start": v(27.5, -28.5) * mm, "end": v(12.5, -28.5) * mm});
            skLineSegment(sketch, "E18.3.2.1", {"start": v(27.5, -11.5) * mm, "end": v(12.5, -11.5) * mm});
            skLineSegment(sketch, "E18.3.2.2", {"start": v(27.5, -24) * mm, "end": v(12.5, -24) * mm});
            skLineSegment(sketch, "E18.3.2.3", {"start": v(29.5, -29.5) * mm, "end": v(10.5, -29.5) * mm, "construction": true});
            skPoint(sketch, "E18.3.2.4", {"position": v(20, -23) * mm});
            skLineSegment(sketch, "E18.3.2.5", {"start": v(29.5, -10.5) * mm, "end": v(10.5, -10.5) * mm, "construction": true});
            skLineSegment(sketch, "E18.3.2.6", {"start": v(27.5, -13.5) * mm, "end": v(12.5, -13.5) * mm});
            skLineSegment(sketch, "E18.3.2.7", {"start": v(29.5, -29.5) * mm, "end": v(29.5, -10.5) * mm, "construction": true});
            skPoint(sketch, "E18.3.2.8", {"position": v(20, -17) * mm});
            skLineSegment(sketch, "E18.3.2.9", {"start": v(27.5, -26.5) * mm, "end": v(12.5, -26.5) * mm});
            skLineSegment(sketch, "E18.3.2.10", {"start": v(27.5, -16) * mm, "end": v(12.5, -16) * mm});
            skLineSegment(sketch, "E18.3.2.11", {"start": v(27.5, -22) * mm, "end": v(12.5, -22) * mm});
            skPoint(sketch, "E18.3.2.12", {"position": v(20, -12.5) * mm});
            skLineSegment(sketch, "E18.3.2.13", {"start": v(10.5, -29.5) * mm, "end": v(10.5, -10.5) * mm, "construction": true});
            skPoint(sketch, "E18.3.2.14", {"position": v(20, -27.5) * mm});
            skLineSegment(sketch, "E18.3.2.15", {"start": v(27.5, -18) * mm, "end": v(12.5, -18) * mm});
            skCircle(sketch, "E18.3.2.16", {"center": v(14.5, -20) * mm, "radius": 1 * mm});
            skCircle(sketch, "E18.3.2.17", {"center": v(25.5, -20) * mm, "radius": 1 * mm});
            skPoint(sketch, "E18.3.2.18", {"position": v(20, -20) * mm});
            skLineSegment(sketch, "E18.3.2.19", {"start": v(12.5, -26.5) * mm, "end": v(12.5, -28.5) * mm});
            skLineSegment(sketch, "E18.3.2.20", {"start": v(27.5, -13.5) * mm, "end": v(27.5, -11.5) * mm});
            skLineSegment(sketch, "E18.3.2.21", {"start": v(12.5, -13.5) * mm, "end": v(12.5, -11.5) * mm});
            skLineSegment(sketch, "E18.3.2.22", {"start": v(27.5, -22) * mm, "end": v(27.5, -24) * mm});
            skLineSegment(sketch, "E18.3.2.23", {"start": v(27.5, -18) * mm, "end": v(27.5, -16) * mm});
            skLineSegment(sketch, "E18.3.2.24", {"start": v(12.5, -18) * mm, "end": v(12.5, -16) * mm});
            skLineSegment(sketch, "E18.3.2.25", {"start": v(27.5, -26.5) * mm, "end": v(27.5, -28.5) * mm});
            skLineSegment(sketch, "E18.3.2.26", {"start": v(12.5, -22) * mm, "end": v(12.5, -24) * mm});
            skLineSegment(sketch, "E18.4.0.0", {"start": v(7.5, 11.5) * mm, "end": v(-7.5, 11.5) * mm});
            skLineSegment(sketch, "E18.4.0.1", {"start": v(7.5, 28.5) * mm, "end": v(-7.5, 28.5) * mm});
            skLineSegment(sketch, "E18.4.0.2", {"start": v(7.5, 16) * mm, "end": v(-7.5, 16) * mm});
            skLineSegment(sketch, "E18.4.0.3", {"start": v(9.5, 10.5) * mm, "end": v(-9.5, 10.5) * mm, "construction": true});
            skPoint(sketch, "E18.4.0.4", {"position": v(0, 17) * mm});
            skLineSegment(sketch, "E18.4.0.5", {"start": v(9.5, 29.5) * mm, "end": v(-9.5, 29.5) * mm, "construction": true});
            skLineSegment(sketch, "E18.4.0.6", {"start": v(7.5, 26.5) * mm, "end": v(-7.5, 26.5) * mm});
            skLineSegment(sketch, "E18.4.0.7", {"start": v(9.5, 10.5) * mm, "end": v(9.5, 29.5) * mm, "construction": true});
            skPoint(sketch, "E18.4.0.8", {"position": v(0, 23) * mm});
            skLineSegment(sketch, "E18.4.0.9", {"start": v(7.5, 13.5) * mm, "end": v(-7.5, 13.5) * mm});
            skLineSegment(sketch, "E18.4.0.10", {"start": v(7.5, 24) * mm, "end": v(-7.5, 24) * mm});
            skLineSegment(sketch, "E18.4.0.11", {"start": v(7.5, 18) * mm, "end": v(-7.5, 18) * mm});
            skPoint(sketch, "E18.4.0.12", {"position": v(0, 27.5) * mm});
            skLineSegment(sketch, "E18.4.0.13", {"start": v(-9.5, 10.5) * mm, "end": v(-9.5, 29.5) * mm, "construction": true});
            skPoint(sketch, "E18.4.0.14", {"position": v(0, 12.5) * mm});
            skLineSegment(sketch, "E18.4.0.15", {"start": v(7.5, 22) * mm, "end": v(-7.5, 22) * mm});
            skCircle(sketch, "E18.4.0.16", {"center": v(-5.5, 20) * mm, "radius": 1 * mm});
            skCircle(sketch, "E18.4.0.17", {"center": v(5.5, 20) * mm, "radius": 1 * mm});
            skPoint(sketch, "E18.4.0.18", {"position": v(0, 20) * mm});
            skLineSegment(sketch, "E18.4.0.19", {"start": v(-7.5, 13.5) * mm, "end": v(-7.5, 11.5) * mm});
            skLineSegment(sketch, "E18.4.0.20", {"start": v(7.5, 26.5) * mm, "end": v(7.5, 28.5) * mm});
            skLineSegment(sketch, "E18.4.0.21", {"start": v(-7.5, 26.5) * mm, "end": v(-7.5, 28.5) * mm});
            skLineSegment(sketch, "E18.4.0.22", {"start": v(7.5, 18) * mm, "end": v(7.5, 16) * mm});
            skLineSegment(sketch, "E18.4.0.23", {"start": v(7.5, 22) * mm, "end": v(7.5, 24) * mm});
            skLineSegment(sketch, "E18.4.0.24", {"start": v(-7.5, 22) * mm, "end": v(-7.5, 24) * mm});
            skLineSegment(sketch, "E18.4.0.25", {"start": v(7.5, 13.5) * mm, "end": v(7.5, 11.5) * mm});
            skLineSegment(sketch, "E18.4.0.26", {"start": v(-7.5, 18) * mm, "end": v(-7.5, 16) * mm});
            skLineSegment(sketch, "E18.4.1.0", {"start": v(7.5, -8.5) * mm, "end": v(-7.5, -8.5) * mm});
            skLineSegment(sketch, "E18.4.1.1", {"start": v(7.5, 8.5) * mm, "end": v(-7.5, 8.5) * mm});
            skLineSegment(sketch, "E18.4.1.2", {"start": v(7.5, -4) * mm, "end": v(-7.5, -4) * mm});
            skLineSegment(sketch, "E18.4.1.3", {"start": v(9.5, -9.5) * mm, "end": v(-9.5, -9.5) * mm, "construction": true});
            skPoint(sketch, "E18.4.1.4", {"position": v(0, -3) * mm});
            skLineSegment(sketch, "E18.4.1.5", {"start": v(9.5, 9.5) * mm, "end": v(-9.5, 9.5) * mm, "construction": true});
            skLineSegment(sketch, "E18.4.1.6", {"start": v(7.5, 6.5) * mm, "end": v(-7.5, 6.5) * mm});
            skLineSegment(sketch, "E18.4.1.7", {"start": v(9.5, -9.5) * mm, "end": v(9.5, 9.5) * mm, "construction": true});
            skPoint(sketch, "E18.4.1.8", {"position": v(0, 3) * mm});
            skLineSegment(sketch, "E18.4.1.9", {"start": v(7.5, -6.5) * mm, "end": v(-7.5, -6.5) * mm});
            skLineSegment(sketch, "E18.4.1.10", {"start": v(7.5, 4) * mm, "end": v(-7.5, 4) * mm});
            skLineSegment(sketch, "E18.4.1.11", {"start": v(7.5, -2) * mm, "end": v(-7.5, -2) * mm});
            skPoint(sketch, "E18.4.1.12", {"position": v(0, 7.5) * mm});
            skLineSegment(sketch, "E18.4.1.13", {"start": v(-9.5, -9.5) * mm, "end": v(-9.5, 9.5) * mm, "construction": true});
            skPoint(sketch, "E18.4.1.14", {"position": v(0, -7.5) * mm});
            skLineSegment(sketch, "E18.4.1.15", {"start": v(7.5, 2) * mm, "end": v(-7.5, 2) * mm});
            skCircle(sketch, "E18.4.1.16", {"center": v(-5.5, 0) * mm, "radius": 1 * mm});
            skCircle(sketch, "E18.4.1.17", {"center": v(5.5, 0) * mm, "radius": 1 * mm});
            skPoint(sketch, "E18.4.1.18", {"position": v(0, 0) * mm});
            skLineSegment(sketch, "E18.4.1.19", {"start": v(-7.5, -6.5) * mm, "end": v(-7.5, -8.5) * mm});
            skLineSegment(sketch, "E18.4.1.20", {"start": v(7.5, 6.5) * mm, "end": v(7.5, 8.5) * mm});
            skLineSegment(sketch, "E18.4.1.21", {"start": v(-7.5, 6.5) * mm, "end": v(-7.5, 8.5) * mm});
            skLineSegment(sketch, "E18.4.1.22", {"start": v(7.5, -2) * mm, "end": v(7.5, -4) * mm});
            skLineSegment(sketch, "E18.4.1.23", {"start": v(7.5, 2) * mm, "end": v(7.5, 4) * mm});
            skLineSegment(sketch, "E18.4.1.24", {"start": v(-7.5, 2) * mm, "end": v(-7.5, 4) * mm});
            skLineSegment(sketch, "E18.4.1.25", {"start": v(7.5, -6.5) * mm, "end": v(7.5, -8.5) * mm});
            skLineSegment(sketch, "E18.4.1.26", {"start": v(-7.5, -2) * mm, "end": v(-7.5, -4) * mm});
            skLineSegment(sketch, "E18.4.2.0", {"start": v(7.5, -28.5) * mm, "end": v(-7.5, -28.5) * mm});
            skLineSegment(sketch, "E18.4.2.1", {"start": v(7.5, -11.5) * mm, "end": v(-7.5, -11.5) * mm});
            skLineSegment(sketch, "E18.4.2.2", {"start": v(7.5, -24) * mm, "end": v(-7.5, -24) * mm});
            skLineSegment(sketch, "E18.4.2.3", {"start": v(9.5, -29.5) * mm, "end": v(-9.5, -29.5) * mm, "construction": true});
            skPoint(sketch, "E18.4.2.4", {"position": v(0, -23) * mm});
            skLineSegment(sketch, "E18.4.2.5", {"start": v(9.5, -10.5) * mm, "end": v(-9.5, -10.5) * mm, "construction": true});
            skLineSegment(sketch, "E18.4.2.6", {"start": v(7.5, -13.5) * mm, "end": v(-7.5, -13.5) * mm});
            skLineSegment(sketch, "E18.4.2.7", {"start": v(9.5, -29.5) * mm, "end": v(9.5, -10.5) * mm, "construction": true});
            skPoint(sketch, "E18.4.2.8", {"position": v(0, -17) * mm});
            skLineSegment(sketch, "E18.4.2.9", {"start": v(7.5, -26.5) * mm, "end": v(-7.5, -26.5) * mm});
            skLineSegment(sketch, "E18.4.2.10", {"start": v(7.5, -16) * mm, "end": v(-7.5, -16) * mm});
            skLineSegment(sketch, "E18.4.2.11", {"start": v(7.5, -22) * mm, "end": v(-7.5, -22) * mm});
            skPoint(sketch, "E18.4.2.12", {"position": v(0, -12.5) * mm});
            skLineSegment(sketch, "E18.4.2.13", {"start": v(-9.5, -29.5) * mm, "end": v(-9.5, -10.5) * mm, "construction": true});
            skPoint(sketch, "E18.4.2.14", {"position": v(0, -27.5) * mm});
            skLineSegment(sketch, "E18.4.2.15", {"start": v(7.5, -18) * mm, "end": v(-7.5, -18) * mm});
            skCircle(sketch, "E18.4.2.16", {"center": v(-5.5, -20) * mm, "radius": 1 * mm});
            skCircle(sketch, "E18.4.2.17", {"center": v(5.5, -20) * mm, "radius": 1 * mm});
            skPoint(sketch, "E18.4.2.18", {"position": v(0, -20) * mm});
            skLineSegment(sketch, "E18.4.2.19", {"start": v(-7.5, -26.5) * mm, "end": v(-7.5, -28.5) * mm});
            skLineSegment(sketch, "E18.4.2.20", {"start": v(7.5, -13.5) * mm, "end": v(7.5, -11.5) * mm});
            skLineSegment(sketch, "E18.4.2.21", {"start": v(-7.5, -13.5) * mm, "end": v(-7.5, -11.5) * mm});
            skLineSegment(sketch, "E18.4.2.22", {"start": v(7.5, -22) * mm, "end": v(7.5, -24) * mm});
            skLineSegment(sketch, "E18.4.2.23", {"start": v(7.5, -18) * mm, "end": v(7.5, -16) * mm});
            skLineSegment(sketch, "E18.4.2.24", {"start": v(-7.5, -18) * mm, "end": v(-7.5, -16) * mm});
            skLineSegment(sketch, "E18.4.2.25", {"start": v(7.5, -26.5) * mm, "end": v(7.5, -28.5) * mm});
            skLineSegment(sketch, "E18.4.2.26", {"start": v(-7.5, -22) * mm, "end": v(-7.5, -24) * mm});
            skLineSegment(sketch, "E18.5.0.0", {"start": v(-12.5, 11.5) * mm, "end": v(-27.5, 11.5) * mm});
            skLineSegment(sketch, "E18.5.0.1", {"start": v(-12.5, 28.5) * mm, "end": v(-27.5, 28.5) * mm});
            skLineSegment(sketch, "E18.5.0.2", {"start": v(-12.5, 16) * mm, "end": v(-27.5, 16) * mm});
            skLineSegment(sketch, "E18.5.0.3", {"start": v(-10.5, 10.5) * mm, "end": v(-29.5, 10.5) * mm, "construction": true});
            skPoint(sketch, "E18.5.0.4", {"position": v(-20, 17) * mm});
            skLineSegment(sketch, "E18.5.0.5", {"start": v(-10.5, 29.5) * mm, "end": v(-29.5, 29.5) * mm, "construction": true});
            skLineSegment(sketch, "E18.5.0.6", {"start": v(-12.5, 26.5) * mm, "end": v(-27.5, 26.5) * mm});
            skLineSegment(sketch, "E18.5.0.7", {"start": v(-10.5, 10.5) * mm, "end": v(-10.5, 29.5) * mm, "construction": true});
            skPoint(sketch, "E18.5.0.8", {"position": v(-20, 23) * mm});
            skLineSegment(sketch, "E18.5.0.9", {"start": v(-12.5, 13.5) * mm, "end": v(-27.5, 13.5) * mm});
            skLineSegment(sketch, "E18.5.0.10", {"start": v(-12.5, 24) * mm, "end": v(-27.5, 24) * mm});
            skLineSegment(sketch, "E18.5.0.11", {"start": v(-12.5, 18) * mm, "end": v(-27.5, 18) * mm});
            skPoint(sketch, "E18.5.0.12", {"position": v(-20, 27.5) * mm});
            skLineSegment(sketch, "E18.5.0.13", {"start": v(-29.5, 10.5) * mm, "end": v(-29.5, 29.5) * mm, "construction": true});
            skPoint(sketch, "E18.5.0.14", {"position": v(-20, 12.5) * mm});
            skLineSegment(sketch, "E18.5.0.15", {"start": v(-12.5, 22) * mm, "end": v(-27.5, 22) * mm});
            skCircle(sketch, "E18.5.0.16", {"center": v(-25.5, 20) * mm, "radius": 1 * mm});
            skCircle(sketch, "E18.5.0.17", {"center": v(-14.5, 20) * mm, "radius": 1 * mm});
            skPoint(sketch, "E18.5.0.18", {"position": v(-20, 20) * mm});
            skLineSegment(sketch, "E18.5.0.19", {"start": v(-27.5, 13.5) * mm, "end": v(-27.5, 11.5) * mm});
            skLineSegment(sketch, "E18.5.0.20", {"start": v(-12.5, 26.5) * mm, "end": v(-12.5, 28.5) * mm});
            skLineSegment(sketch, "E18.5.0.21", {"start": v(-27.5, 26.5) * mm, "end": v(-27.5, 28.5) * mm});
            skLineSegment(sketch, "E18.5.0.22", {"start": v(-12.5, 18) * mm, "end": v(-12.5, 16) * mm});
            skLineSegment(sketch, "E18.5.0.23", {"start": v(-12.5, 22) * mm, "end": v(-12.5, 24) * mm});
            skLineSegment(sketch, "E18.5.0.24", {"start": v(-27.5, 22) * mm, "end": v(-27.5, 24) * mm});
            skLineSegment(sketch, "E18.5.0.25", {"start": v(-12.5, 13.5) * mm, "end": v(-12.5, 11.5) * mm});
            skLineSegment(sketch, "E18.5.0.26", {"start": v(-27.5, 18) * mm, "end": v(-27.5, 16) * mm});
            skLineSegment(sketch, "E18.5.1.0", {"start": v(-12.5, -8.5) * mm, "end": v(-27.5, -8.5) * mm});
            skLineSegment(sketch, "E18.5.1.1", {"start": v(-12.5, 8.5) * mm, "end": v(-27.5, 8.5) * mm});
            skLineSegment(sketch, "E18.5.1.2", {"start": v(-12.5, -4) * mm, "end": v(-27.5, -4) * mm});
            skLineSegment(sketch, "E18.5.1.3", {"start": v(-10.5, -9.5) * mm, "end": v(-29.5, -9.5) * mm, "construction": true});
            skPoint(sketch, "E18.5.1.4", {"position": v(-20, -3) * mm});
            skLineSegment(sketch, "E18.5.1.5", {"start": v(-10.5, 9.5) * mm, "end": v(-29.5, 9.5) * mm, "construction": true});
            skLineSegment(sketch, "E18.5.1.6", {"start": v(-12.5, 6.5) * mm, "end": v(-27.5, 6.5) * mm});
            skLineSegment(sketch, "E18.5.1.7", {"start": v(-10.5, -9.5) * mm, "end": v(-10.5, 9.5) * mm, "construction": true});
            skPoint(sketch, "E18.5.1.8", {"position": v(-20, 3) * mm});
            skLineSegment(sketch, "E18.5.1.9", {"start": v(-12.5, -6.5) * mm, "end": v(-27.5, -6.5) * mm});
            skLineSegment(sketch, "E18.5.1.10", {"start": v(-12.5, 4) * mm, "end": v(-27.5, 4) * mm});
            skLineSegment(sketch, "E18.5.1.11", {"start": v(-12.5, -2) * mm, "end": v(-27.5, -2) * mm});
            skPoint(sketch, "E18.5.1.12", {"position": v(-20, 7.5) * mm});
            skLineSegment(sketch, "E18.5.1.13", {"start": v(-29.5, -9.5) * mm, "end": v(-29.5, 9.5) * mm, "construction": true});
            skPoint(sketch, "E18.5.1.14", {"position": v(-20, -7.5) * mm});
            skLineSegment(sketch, "E18.5.1.15", {"start": v(-12.5, 2) * mm, "end": v(-27.5, 2) * mm});
            skCircle(sketch, "E18.5.1.16", {"center": v(-25.5, 0) * mm, "radius": 1 * mm});
            skCircle(sketch, "E18.5.1.17", {"center": v(-14.5, 0) * mm, "radius": 1 * mm});
            skPoint(sketch, "E18.5.1.18", {"position": v(-20, 0) * mm});
            skLineSegment(sketch, "E18.5.1.19", {"start": v(-27.5, -6.5) * mm, "end": v(-27.5, -8.5) * mm});
            skLineSegment(sketch, "E18.5.1.20", {"start": v(-12.5, 6.5) * mm, "end": v(-12.5, 8.5) * mm});
            skLineSegment(sketch, "E18.5.1.21", {"start": v(-27.5, 6.5) * mm, "end": v(-27.5, 8.5) * mm});
            skLineSegment(sketch, "E18.5.1.22", {"start": v(-12.5, -2) * mm, "end": v(-12.5, -4) * mm});
            skLineSegment(sketch, "E18.5.1.23", {"start": v(-12.5, 2) * mm, "end": v(-12.5, 4) * mm});
            skLineSegment(sketch, "E18.5.1.24", {"start": v(-27.5, 2) * mm, "end": v(-27.5, 4) * mm});
            skLineSegment(sketch, "E18.5.1.25", {"start": v(-12.5, -6.5) * mm, "end": v(-12.5, -8.5) * mm});
            skLineSegment(sketch, "E18.5.1.26", {"start": v(-27.5, -2) * mm, "end": v(-27.5, -4) * mm});
            skLineSegment(sketch, "E18.5.2.0", {"start": v(-12.5, -28.5) * mm, "end": v(-27.5, -28.5) * mm});
            skLineSegment(sketch, "E18.5.2.1", {"start": v(-12.5, -11.5) * mm, "end": v(-27.5, -11.5) * mm});
            skLineSegment(sketch, "E18.5.2.2", {"start": v(-12.5, -24) * mm, "end": v(-27.5, -24) * mm});
            skLineSegment(sketch, "E18.5.2.3", {"start": v(-10.5, -29.5) * mm, "end": v(-29.5, -29.5) * mm, "construction": true});
            skPoint(sketch, "E18.5.2.4", {"position": v(-20, -23) * mm});
            skLineSegment(sketch, "E18.5.2.5", {"start": v(-10.5, -10.5) * mm, "end": v(-29.5, -10.5) * mm, "construction": true});
            skLineSegment(sketch, "E18.5.2.6", {"start": v(-12.5, -13.5) * mm, "end": v(-27.5, -13.5) * mm});
            skLineSegment(sketch, "E18.5.2.7", {"start": v(-10.5, -29.5) * mm, "end": v(-10.5, -10.5) * mm, "construction": true});
            skPoint(sketch, "E18.5.2.8", {"position": v(-20, -17) * mm});
            skLineSegment(sketch, "E18.5.2.9", {"start": v(-12.5, -26.5) * mm, "end": v(-27.5, -26.5) * mm});
            skLineSegment(sketch, "E18.5.2.10", {"start": v(-12.5, -16) * mm, "end": v(-27.5, -16) * mm});
            skLineSegment(sketch, "E18.5.2.11", {"start": v(-12.5, -22) * mm, "end": v(-27.5, -22) * mm});
            skPoint(sketch, "E18.5.2.12", {"position": v(-20, -12.5) * mm});
            skLineSegment(sketch, "E18.5.2.13", {"start": v(-29.5, -29.5) * mm, "end": v(-29.5, -10.5) * mm, "construction": true});
            skPoint(sketch, "E18.5.2.14", {"position": v(-20, -27.5) * mm});
            skLineSegment(sketch, "E18.5.2.15", {"start": v(-12.5, -18) * mm, "end": v(-27.5, -18) * mm});
            skCircle(sketch, "E18.5.2.16", {"center": v(-25.5, -20) * mm, "radius": 1 * mm});
            skCircle(sketch, "E18.5.2.17", {"center": v(-14.5, -20) * mm, "radius": 1 * mm});
            skPoint(sketch, "E18.5.2.18", {"position": v(-20, -20) * mm});
            skLineSegment(sketch, "E18.5.2.19", {"start": v(-27.5, -26.5) * mm, "end": v(-27.5, -28.5) * mm});
            skLineSegment(sketch, "E18.5.2.20", {"start": v(-12.5, -13.5) * mm, "end": v(-12.5, -11.5) * mm});
            skLineSegment(sketch, "E18.5.2.21", {"start": v(-27.5, -13.5) * mm, "end": v(-27.5, -11.5) * mm});
            skLineSegment(sketch, "E18.5.2.22", {"start": v(-12.5, -22) * mm, "end": v(-12.5, -24) * mm});
            skLineSegment(sketch, "E18.5.2.23", {"start": v(-12.5, -18) * mm, "end": v(-12.5, -16) * mm});
            skLineSegment(sketch, "E18.5.2.24", {"start": v(-27.5, -18) * mm, "end": v(-27.5, -16) * mm});
            skLineSegment(sketch, "E18.5.2.25", {"start": v(-12.5, -26.5) * mm, "end": v(-12.5, -28.5) * mm});
            skLineSegment(sketch, "E18.5.2.26", {"start": v(-27.5, -22) * mm, "end": v(-27.5, -24) * mm});
            skLineSegment(sketch, "E18.6.0.0", {"start": v(-32.5, 11.5) * mm, "end": v(-47.5, 11.5) * mm});
            skLineSegment(sketch, "E18.6.0.1", {"start": v(-32.5, 28.5) * mm, "end": v(-47.5, 28.5) * mm});
            skLineSegment(sketch, "E18.6.0.2", {"start": v(-32.5, 16) * mm, "end": v(-47.5, 16) * mm});
            skLineSegment(sketch, "E18.6.0.3", {"start": v(-30.5, 10.5) * mm, "end": v(-49.5, 10.5) * mm, "construction": true});
            skPoint(sketch, "E18.6.0.4", {"position": v(-40, 17) * mm});
            skLineSegment(sketch, "E18.6.0.5", {"start": v(-30.5, 29.5) * mm, "end": v(-49.5, 29.5) * mm, "construction": true});
            skLineSegment(sketch, "E18.6.0.6", {"start": v(-32.5, 26.5) * mm, "end": v(-47.5, 26.5) * mm});
            skLineSegment(sketch, "E18.6.0.7", {"start": v(-30.5, 10.5) * mm, "end": v(-30.5, 29.5) * mm, "construction": true});
            skPoint(sketch, "E18.6.0.8", {"position": v(-40, 23) * mm});
            skLineSegment(sketch, "E18.6.0.9", {"start": v(-32.5, 13.5) * mm, "end": v(-47.5, 13.5) * mm});
            skLineSegment(sketch, "E18.6.0.10", {"start": v(-32.5, 24) * mm, "end": v(-47.5, 24) * mm});
            skLineSegment(sketch, "E18.6.0.11", {"start": v(-32.5, 18) * mm, "end": v(-47.5, 18) * mm});
            skPoint(sketch, "E18.6.0.12", {"position": v(-40, 27.5) * mm});
            skLineSegment(sketch, "E18.6.0.13", {"start": v(-49.5, 10.5) * mm, "end": v(-49.5, 29.5) * mm, "construction": true});
            skPoint(sketch, "E18.6.0.14", {"position": v(-40, 12.5) * mm});
            skLineSegment(sketch, "E18.6.0.15", {"start": v(-32.5, 22) * mm, "end": v(-47.5, 22) * mm});
            skCircle(sketch, "E18.6.0.16", {"center": v(-45.5, 20) * mm, "radius": 1 * mm});
            skCircle(sketch, "E18.6.0.17", {"center": v(-34.5, 20) * mm, "radius": 1 * mm});
            skPoint(sketch, "E18.6.0.18", {"position": v(-40, 20) * mm});
            skLineSegment(sketch, "E18.6.0.19", {"start": v(-47.5, 13.5) * mm, "end": v(-47.5, 11.5) * mm});
            skLineSegment(sketch, "E18.6.0.20", {"start": v(-32.5, 26.5) * mm, "end": v(-32.5, 28.5) * mm});
            skLineSegment(sketch, "E18.6.0.21", {"start": v(-47.5, 26.5) * mm, "end": v(-47.5, 28.5) * mm});
            skLineSegment(sketch, "E18.6.0.22", {"start": v(-32.5, 18) * mm, "end": v(-32.5, 16) * mm});
            skLineSegment(sketch, "E18.6.0.23", {"start": v(-32.5, 22) * mm, "end": v(-32.5, 24) * mm});
            skLineSegment(sketch, "E18.6.0.24", {"start": v(-47.5, 22) * mm, "end": v(-47.5, 24) * mm});
            skLineSegment(sketch, "E18.6.0.25", {"start": v(-32.5, 13.5) * mm, "end": v(-32.5, 11.5) * mm});
            skLineSegment(sketch, "E18.6.0.26", {"start": v(-47.5, 18) * mm, "end": v(-47.5, 16) * mm});
            skLineSegment(sketch, "E18.6.1.0", {"start": v(-32.5, -8.5) * mm, "end": v(-47.5, -8.5) * mm});
            skLineSegment(sketch, "E18.6.1.1", {"start": v(-32.5, 8.5) * mm, "end": v(-47.5, 8.5) * mm});
            skLineSegment(sketch, "E18.6.1.2", {"start": v(-32.5, -4) * mm, "end": v(-47.5, -4) * mm});
            skLineSegment(sketch, "E18.6.1.3", {"start": v(-30.5, -9.5) * mm, "end": v(-49.5, -9.5) * mm, "construction": true});
            skPoint(sketch, "E18.6.1.4", {"position": v(-40, -3) * mm});
            skLineSegment(sketch, "E18.6.1.5", {"start": v(-30.5, 9.5) * mm, "end": v(-49.5, 9.5) * mm, "construction": true});
            skLineSegment(sketch, "E18.6.1.6", {"start": v(-32.5, 6.5) * mm, "end": v(-47.5, 6.5) * mm});
            skLineSegment(sketch, "E18.6.1.7", {"start": v(-30.5, -9.5) * mm, "end": v(-30.5, 9.5) * mm, "construction": true});
            skPoint(sketch, "E18.6.1.8", {"position": v(-40, 3) * mm});
            skLineSegment(sketch, "E18.6.1.9", {"start": v(-32.5, -6.5) * mm, "end": v(-47.5, -6.5) * mm});
            skLineSegment(sketch, "E18.6.1.10", {"start": v(-32.5, 4) * mm, "end": v(-47.5, 4) * mm});
            skLineSegment(sketch, "E18.6.1.11", {"start": v(-32.5, -2) * mm, "end": v(-47.5, -2) * mm});
            skPoint(sketch, "E18.6.1.12", {"position": v(-40, 7.5) * mm});
            skLineSegment(sketch, "E18.6.1.13", {"start": v(-49.5, -9.5) * mm, "end": v(-49.5, 9.5) * mm, "construction": true});
            skPoint(sketch, "E18.6.1.14", {"position": v(-40, -7.5) * mm});
            skLineSegment(sketch, "E18.6.1.15", {"start": v(-32.5, 2) * mm, "end": v(-47.5, 2) * mm});
            skCircle(sketch, "E18.6.1.16", {"center": v(-45.5, 0) * mm, "radius": 1 * mm});
            skCircle(sketch, "E18.6.1.17", {"center": v(-34.5, 0) * mm, "radius": 1 * mm});
            skPoint(sketch, "E18.6.1.18", {"position": v(-40, 0) * mm});
            skLineSegment(sketch, "E18.6.1.19", {"start": v(-47.5, -6.5) * mm, "end": v(-47.5, -8.5) * mm});
            skLineSegment(sketch, "E18.6.1.20", {"start": v(-32.5, 6.5) * mm, "end": v(-32.5, 8.5) * mm});
            skLineSegment(sketch, "E18.6.1.21", {"start": v(-47.5, 6.5) * mm, "end": v(-47.5, 8.5) * mm});
            skLineSegment(sketch, "E18.6.1.22", {"start": v(-32.5, -2) * mm, "end": v(-32.5, -4) * mm});
            skLineSegment(sketch, "E18.6.1.23", {"start": v(-32.5, 2) * mm, "end": v(-32.5, 4) * mm});
            skLineSegment(sketch, "E18.6.1.24", {"start": v(-47.5, 2) * mm, "end": v(-47.5, 4) * mm});
            skLineSegment(sketch, "E18.6.1.25", {"start": v(-32.5, -6.5) * mm, "end": v(-32.5, -8.5) * mm});
            skLineSegment(sketch, "E18.6.1.26", {"start": v(-47.5, -2) * mm, "end": v(-47.5, -4) * mm});
            skLineSegment(sketch, "E18.6.2.0", {"start": v(-32.5, -28.5) * mm, "end": v(-47.5, -28.5) * mm});
            skLineSegment(sketch, "E18.6.2.1", {"start": v(-32.5, -11.5) * mm, "end": v(-47.5, -11.5) * mm});
            skLineSegment(sketch, "E18.6.2.2", {"start": v(-32.5, -24) * mm, "end": v(-47.5, -24) * mm});
            skLineSegment(sketch, "E18.6.2.3", {"start": v(-30.5, -29.5) * mm, "end": v(-49.5, -29.5) * mm, "construction": true});
            skPoint(sketch, "E18.6.2.4", {"position": v(-40, -23) * mm});
            skLineSegment(sketch, "E18.6.2.5", {"start": v(-30.5, -10.5) * mm, "end": v(-49.5, -10.5) * mm, "construction": true});
            skLineSegment(sketch, "E18.6.2.6", {"start": v(-32.5, -13.5) * mm, "end": v(-47.5, -13.5) * mm});
            skLineSegment(sketch, "E18.6.2.7", {"start": v(-30.5, -29.5) * mm, "end": v(-30.5, -10.5) * mm, "construction": true});
            skPoint(sketch, "E18.6.2.8", {"position": v(-40, -17) * mm});
            skLineSegment(sketch, "E18.6.2.9", {"start": v(-32.5, -26.5) * mm, "end": v(-47.5, -26.5) * mm});
            skLineSegment(sketch, "E18.6.2.10", {"start": v(-32.5, -16) * mm, "end": v(-47.5, -16) * mm});
            skLineSegment(sketch, "E18.6.2.11", {"start": v(-32.5, -22) * mm, "end": v(-47.5, -22) * mm});
            skPoint(sketch, "E18.6.2.12", {"position": v(-40, -12.5) * mm});
            skLineSegment(sketch, "E18.6.2.13", {"start": v(-49.5, -29.5) * mm, "end": v(-49.5, -10.5) * mm, "construction": true});
            skPoint(sketch, "E18.6.2.14", {"position": v(-40, -27.5) * mm});
            skLineSegment(sketch, "E18.6.2.15", {"start": v(-32.5, -18) * mm, "end": v(-47.5, -18) * mm});
            skCircle(sketch, "E18.6.2.16", {"center": v(-45.5, -20) * mm, "radius": 1 * mm});
            skCircle(sketch, "E18.6.2.17", {"center": v(-34.5, -20) * mm, "radius": 1 * mm});
            skPoint(sketch, "E18.6.2.18", {"position": v(-40, -20) * mm});
            skLineSegment(sketch, "E18.6.2.19", {"start": v(-47.5, -26.5) * mm, "end": v(-47.5, -28.5) * mm});
            skLineSegment(sketch, "E18.6.2.20", {"start": v(-32.5, -13.5) * mm, "end": v(-32.5, -11.5) * mm});
            skLineSegment(sketch, "E18.6.2.21", {"start": v(-47.5, -13.5) * mm, "end": v(-47.5, -11.5) * mm});
            skLineSegment(sketch, "E18.6.2.22", {"start": v(-32.5, -22) * mm, "end": v(-32.5, -24) * mm});
            skLineSegment(sketch, "E18.6.2.23", {"start": v(-32.5, -18) * mm, "end": v(-32.5, -16) * mm});
            skLineSegment(sketch, "E18.6.2.24", {"start": v(-47.5, -18) * mm, "end": v(-47.5, -16) * mm});
            skLineSegment(sketch, "E18.6.2.25", {"start": v(-32.5, -26.5) * mm, "end": v(-32.5, -28.5) * mm});
            skLineSegment(sketch, "E18.6.2.26", {"start": v(-47.5, -22) * mm, "end": v(-47.5, -24) * mm});
            skLineSegment(sketch, "E18.7.0.0", {"start": v(-52.5, 11.5) * mm, "end": v(-67.5, 11.5) * mm});
            skLineSegment(sketch, "E18.7.0.1", {"start": v(-52.5, 28.5) * mm, "end": v(-67.5, 28.5) * mm});
            skLineSegment(sketch, "E18.7.0.2", {"start": v(-52.5, 16) * mm, "end": v(-67.5, 16) * mm});
            skLineSegment(sketch, "E18.7.0.3", {"start": v(-50.5, 10.5) * mm, "end": v(-69.5, 10.5) * mm, "construction": true});
            skPoint(sketch, "E18.7.0.4", {"position": v(-60, 17) * mm});
            skLineSegment(sketch, "E18.7.0.5", {"start": v(-50.5, 29.5) * mm, "end": v(-69.5, 29.5) * mm, "construction": true});
            skLineSegment(sketch, "E18.7.0.6", {"start": v(-52.5, 26.5) * mm, "end": v(-67.5, 26.5) * mm});
            skLineSegment(sketch, "E18.7.0.7", {"start": v(-50.5, 10.5) * mm, "end": v(-50.5, 29.5) * mm, "construction": true});
            skPoint(sketch, "E18.7.0.8", {"position": v(-60, 23) * mm});
            skLineSegment(sketch, "E18.7.0.9", {"start": v(-52.5, 13.5) * mm, "end": v(-67.5, 13.5) * mm});
            skLineSegment(sketch, "E18.7.0.10", {"start": v(-52.5, 24) * mm, "end": v(-67.5, 24) * mm});
            skLineSegment(sketch, "E18.7.0.11", {"start": v(-52.5, 18) * mm, "end": v(-67.5, 18) * mm});
            skPoint(sketch, "E18.7.0.12", {"position": v(-60, 27.5) * mm});
            skLineSegment(sketch, "E18.7.0.13", {"start": v(-69.5, 10.5) * mm, "end": v(-69.5, 29.5) * mm, "construction": true});
            skPoint(sketch, "E18.7.0.14", {"position": v(-60, 12.5) * mm});
            skLineSegment(sketch, "E18.7.0.15", {"start": v(-52.5, 22) * mm, "end": v(-67.5, 22) * mm});
            skCircle(sketch, "E18.7.0.16", {"center": v(-65.5, 20) * mm, "radius": 1 * mm});
            skCircle(sketch, "E18.7.0.17", {"center": v(-54.5, 20) * mm, "radius": 1 * mm});
            skPoint(sketch, "E18.7.0.18", {"position": v(-60, 20) * mm});
            skLineSegment(sketch, "E18.7.0.19", {"start": v(-67.5, 13.5) * mm, "end": v(-67.5, 11.5) * mm});
            skLineSegment(sketch, "E18.7.0.20", {"start": v(-52.5, 26.5) * mm, "end": v(-52.5, 28.5) * mm});
            skLineSegment(sketch, "E18.7.0.21", {"start": v(-67.5, 26.5) * mm, "end": v(-67.5, 28.5) * mm});
            skLineSegment(sketch, "E18.7.0.22", {"start": v(-52.5, 18) * mm, "end": v(-52.5, 16) * mm});
            skLineSegment(sketch, "E18.7.0.23", {"start": v(-52.5, 22) * mm, "end": v(-52.5, 24) * mm});
            skLineSegment(sketch, "E18.7.0.24", {"start": v(-67.5, 22) * mm, "end": v(-67.5, 24) * mm});
            skLineSegment(sketch, "E18.7.0.25", {"start": v(-52.5, 13.5) * mm, "end": v(-52.5, 11.5) * mm});
            skLineSegment(sketch, "E18.7.0.26", {"start": v(-67.5, 18) * mm, "end": v(-67.5, 16) * mm});
            skLineSegment(sketch, "E18.7.1.0", {"start": v(-52.5, -8.5) * mm, "end": v(-67.5, -8.5) * mm});
            skLineSegment(sketch, "E18.7.1.1", {"start": v(-52.5, 8.5) * mm, "end": v(-67.5, 8.5) * mm});
            skLineSegment(sketch, "E18.7.1.2", {"start": v(-52.5, -4) * mm, "end": v(-67.5, -4) * mm});
            skLineSegment(sketch, "E18.7.1.3", {"start": v(-50.5, -9.5) * mm, "end": v(-69.5, -9.5) * mm, "construction": true});
            skPoint(sketch, "E18.7.1.4", {"position": v(-60, -3) * mm});
            skLineSegment(sketch, "E18.7.1.5", {"start": v(-50.5, 9.5) * mm, "end": v(-69.5, 9.5) * mm, "construction": true});
            skLineSegment(sketch, "E18.7.1.6", {"start": v(-52.5, 6.5) * mm, "end": v(-67.5, 6.5) * mm});
            skLineSegment(sketch, "E18.7.1.7", {"start": v(-50.5, -9.5) * mm, "end": v(-50.5, 9.5) * mm, "construction": true});
            skPoint(sketch, "E18.7.1.8", {"position": v(-60, 3) * mm});
            skLineSegment(sketch, "E18.7.1.9", {"start": v(-52.5, -6.5) * mm, "end": v(-67.5, -6.5) * mm});
            skLineSegment(sketch, "E18.7.1.10", {"start": v(-52.5, 4) * mm, "end": v(-67.5, 4) * mm});
            skLineSegment(sketch, "E18.7.1.11", {"start": v(-52.5, -2) * mm, "end": v(-67.5, -2) * mm});
            skPoint(sketch, "E18.7.1.12", {"position": v(-60, 7.5) * mm});
            skLineSegment(sketch, "E18.7.1.13", {"start": v(-69.5, -9.5) * mm, "end": v(-69.5, 9.5) * mm, "construction": true});
            skPoint(sketch, "E18.7.1.14", {"position": v(-60, -7.5) * mm});
            skLineSegment(sketch, "E18.7.1.15", {"start": v(-52.5, 2) * mm, "end": v(-67.5, 2) * mm});
            skCircle(sketch, "E18.7.1.16", {"center": v(-65.5, 0) * mm, "radius": 1 * mm});
            skCircle(sketch, "E18.7.1.17", {"center": v(-54.5, 0) * mm, "radius": 1 * mm});
            skPoint(sketch, "E18.7.1.18", {"position": v(-60, 0) * mm});
            skLineSegment(sketch, "E18.7.1.19", {"start": v(-67.5, -6.5) * mm, "end": v(-67.5, -8.5) * mm});
            skLineSegment(sketch, "E18.7.1.20", {"start": v(-52.5, 6.5) * mm, "end": v(-52.5, 8.5) * mm});
            skLineSegment(sketch, "E18.7.1.21", {"start": v(-67.5, 6.5) * mm, "end": v(-67.5, 8.5) * mm});
            skLineSegment(sketch, "E18.7.1.22", {"start": v(-52.5, -2) * mm, "end": v(-52.5, -4) * mm});
            skLineSegment(sketch, "E18.7.1.23", {"start": v(-52.5, 2) * mm, "end": v(-52.5, 4) * mm});
            skLineSegment(sketch, "E18.7.1.24", {"start": v(-67.5, 2) * mm, "end": v(-67.5, 4) * mm});
            skLineSegment(sketch, "E18.7.1.25", {"start": v(-52.5, -6.5) * mm, "end": v(-52.5, -8.5) * mm});
            skLineSegment(sketch, "E18.7.1.26", {"start": v(-67.5, -2) * mm, "end": v(-67.5, -4) * mm});
            skLineSegment(sketch, "E18.7.2.0", {"start": v(-52.5, -28.5) * mm, "end": v(-67.5, -28.5) * mm});
            skLineSegment(sketch, "E18.7.2.1", {"start": v(-52.5, -11.5) * mm, "end": v(-67.5, -11.5) * mm});
            skLineSegment(sketch, "E18.7.2.2", {"start": v(-52.5, -24) * mm, "end": v(-67.5, -24) * mm});
            skLineSegment(sketch, "E18.7.2.3", {"start": v(-50.5, -29.5) * mm, "end": v(-69.5, -29.5) * mm, "construction": true});
            skPoint(sketch, "E18.7.2.4", {"position": v(-60, -23) * mm});
            skLineSegment(sketch, "E18.7.2.5", {"start": v(-50.5, -10.5) * mm, "end": v(-69.5, -10.5) * mm, "construction": true});
            skLineSegment(sketch, "E18.7.2.6", {"start": v(-52.5, -13.5) * mm, "end": v(-67.5, -13.5) * mm});
            skLineSegment(sketch, "E18.7.2.7", {"start": v(-50.5, -29.5) * mm, "end": v(-50.5, -10.5) * mm, "construction": true});
            skPoint(sketch, "E18.7.2.8", {"position": v(-60, -17) * mm});
            skLineSegment(sketch, "E18.7.2.9", {"start": v(-52.5, -26.5) * mm, "end": v(-67.5, -26.5) * mm});
            skLineSegment(sketch, "E18.7.2.10", {"start": v(-52.5, -16) * mm, "end": v(-67.5, -16) * mm});
            skLineSegment(sketch, "E18.7.2.11", {"start": v(-52.5, -22) * mm, "end": v(-67.5, -22) * mm});
            skPoint(sketch, "E18.7.2.12", {"position": v(-60, -12.5) * mm});
            skLineSegment(sketch, "E18.7.2.13", {"start": v(-69.5, -29.5) * mm, "end": v(-69.5, -10.5) * mm, "construction": true});
            skPoint(sketch, "E18.7.2.14", {"position": v(-60, -27.5) * mm});
            skLineSegment(sketch, "E18.7.2.15", {"start": v(-52.5, -18) * mm, "end": v(-67.5, -18) * mm});
            skCircle(sketch, "E18.7.2.16", {"center": v(-65.5, -20) * mm, "radius": 1 * mm});
            skCircle(sketch, "E18.7.2.17", {"center": v(-54.5, -20) * mm, "radius": 1 * mm});
            skPoint(sketch, "E18.7.2.18", {"position": v(-60, -20) * mm});
            skLineSegment(sketch, "E18.7.2.19", {"start": v(-67.5, -26.5) * mm, "end": v(-67.5, -28.5) * mm});
            skLineSegment(sketch, "E18.7.2.20", {"start": v(-52.5, -13.5) * mm, "end": v(-52.5, -11.5) * mm});
            skLineSegment(sketch, "E18.7.2.21", {"start": v(-67.5, -13.5) * mm, "end": v(-67.5, -11.5) * mm});
            skLineSegment(sketch, "E18.7.2.22", {"start": v(-52.5, -22) * mm, "end": v(-52.5, -24) * mm});
            skLineSegment(sketch, "E18.7.2.23", {"start": v(-52.5, -18) * mm, "end": v(-52.5, -16) * mm});
            skLineSegment(sketch, "E18.7.2.24", {"start": v(-67.5, -18) * mm, "end": v(-67.5, -16) * mm});
            skLineSegment(sketch, "E18.7.2.25", {"start": v(-52.5, -26.5) * mm, "end": v(-52.5, -28.5) * mm});
            skLineSegment(sketch, "E18.7.2.26", {"start": v(-67.5, -22) * mm, "end": v(-67.5, -24) * mm});
            skLineSegment(sketch, "E18.8.0.3", {"start": v(-70.5, 10.5) * mm, "end": v(-89.5, 10.5) * mm, "construction": true});
            skLineSegment(sketch, "E18.8.0.5", {"start": v(-70.5, 29.5) * mm, "end": v(-89.5, 29.5) * mm, "construction": true});
            skLineSegment(sketch, "E18.8.0.7", {"start": v(-70.5, 10.5) * mm, "end": v(-70.5, 29.5) * mm, "construction": true});
            skLineSegment(sketch, "E18.8.0.13", {"start": v(-89.5, 10.5) * mm, "end": v(-89.5, 29.5) * mm, "construction": true});
            skPoint(sketch, "E18.8.0.18", {"position": v(-80, 20) * mm});
            skLineSegment(sketch, "E18.8.1.0", {"start": v(-72.5, -8.5) * mm, "end": v(-87.5, -8.5) * mm});
            skLineSegment(sketch, "E18.8.1.1", {"start": v(-72.5, 8.5) * mm, "end": v(-87.5, 8.5) * mm});
            skLineSegment(sketch, "E18.8.1.2", {"start": v(-72.5, -4) * mm, "end": v(-87.5, -4) * mm});
            skLineSegment(sketch, "E18.8.1.3", {"start": v(-70.5, -9.5) * mm, "end": v(-89.5, -9.5) * mm, "construction": true});
            skPoint(sketch, "E18.8.1.4", {"position": v(-80, -3) * mm});
            skLineSegment(sketch, "E18.8.1.5", {"start": v(-70.5, 9.5) * mm, "end": v(-89.5, 9.5) * mm, "construction": true});
            skLineSegment(sketch, "E18.8.1.6", {"start": v(-72.5, 6.5) * mm, "end": v(-87.5, 6.5) * mm});
            skLineSegment(sketch, "E18.8.1.7", {"start": v(-70.5, -9.5) * mm, "end": v(-70.5, 9.5) * mm, "construction": true});
            skPoint(sketch, "E18.8.1.8", {"position": v(-80, 3) * mm});
            skLineSegment(sketch, "E18.8.1.9", {"start": v(-72.5, -6.5) * mm, "end": v(-87.5, -6.5) * mm});
            skLineSegment(sketch, "E18.8.1.10", {"start": v(-72.5, 4) * mm, "end": v(-87.5, 4) * mm});
            skLineSegment(sketch, "E18.8.1.11", {"start": v(-72.5, -2) * mm, "end": v(-87.5, -2) * mm});
            skPoint(sketch, "E18.8.1.12", {"position": v(-80, 7.5) * mm});
            skLineSegment(sketch, "E18.8.1.13", {"start": v(-89.5, -9.5) * mm, "end": v(-89.5, 9.5) * mm, "construction": true});
            skPoint(sketch, "E18.8.1.14", {"position": v(-80, -7.5) * mm});
            skLineSegment(sketch, "E18.8.1.15", {"start": v(-72.5, 2) * mm, "end": v(-87.5, 2) * mm});
            skCircle(sketch, "E18.8.1.16", {"center": v(-85.5, 0) * mm, "radius": 1 * mm});
            skCircle(sketch, "E18.8.1.17", {"center": v(-74.5, 0) * mm, "radius": 1 * mm});
            skPoint(sketch, "E18.8.1.18", {"position": v(-80, 0) * mm});
            skLineSegment(sketch, "E18.8.1.19", {"start": v(-87.5, -6.5) * mm, "end": v(-87.5, -8.5) * mm});
            skLineSegment(sketch, "E18.8.1.20", {"start": v(-72.5, 6.5) * mm, "end": v(-72.5, 8.5) * mm});
            skLineSegment(sketch, "E18.8.1.21", {"start": v(-87.5, 6.5) * mm, "end": v(-87.5, 8.5) * mm});
            skLineSegment(sketch, "E18.8.1.22", {"start": v(-72.5, -2) * mm, "end": v(-72.5, -4) * mm});
            skLineSegment(sketch, "E18.8.1.23", {"start": v(-72.5, 2) * mm, "end": v(-72.5, 4) * mm});
            skLineSegment(sketch, "E18.8.1.24", {"start": v(-87.5, 2) * mm, "end": v(-87.5, 4) * mm});
            skLineSegment(sketch, "E18.8.1.25", {"start": v(-72.5, -6.5) * mm, "end": v(-72.5, -8.5) * mm});
            skLineSegment(sketch, "E18.8.1.26", {"start": v(-87.5, -2) * mm, "end": v(-87.5, -4) * mm});
            skLineSegment(sketch, "E18.8.2.3", {"start": v(-70.5, -29.5) * mm, "end": v(-89.5, -29.5) * mm, "construction": true});
            skLineSegment(sketch, "E18.8.2.5", {"start": v(-70.5, -10.5) * mm, "end": v(-89.5, -10.5) * mm, "construction": true});
            skLineSegment(sketch, "E18.8.2.7", {"start": v(-70.5, -29.5) * mm, "end": v(-70.5, -10.5) * mm, "construction": true});
            skLineSegment(sketch, "E18.8.2.13", {"start": v(-89.5, -29.5) * mm, "end": v(-89.5, -10.5) * mm, "construction": true});
            skPoint(sketch, "E18.8.2.18", {"position": v(-80, -20) * mm});
            skLineSegment(sketch, "E18.direction1", {"start": v(70.5, 10.5) * mm, "end": v(50.5, 10.5) * mm, "construction": true});
            skLineSegment(sketch, "E18.direction2", {"start": v(70.5, 10.5) * mm, "end": v(70.5, -9.5) * mm, "construction": true});
            skCircle(sketch, "E19", {"center": v(-86, 20) * mm, "radius": 1 * mm});
            skCircle(sketch, "E20", {"center": v(-74, 20) * mm, "radius": 1 * mm});
            skLineSegment(sketch, "E21.bottom", {"start": v(-76.5, 21.5) * mm, "end": v(-83.5, 21.5) * mm});
            skLineSegment(sketch, "E21.top", {"start": v(-76.5, 23.5) * mm, "end": v(-83.5, 23.5) * mm});
            skLineSegment(sketch, "E21.left", {"start": v(-76.5, 21.5) * mm, "end": v(-76.5, 23.5) * mm});
            skLineSegment(sketch, "E21.right", {"start": v(-83.5, 21.5) * mm, "end": v(-83.5, 23.5) * mm});
            skPoint(sketch, "E21.middle", {"position": v(-80, 22.5) * mm});
            skLineSegment(sketch, "E22.bottom", {"start": v(-76.5, 18.5) * mm, "end": v(-83.5, 18.5) * mm});
            skLineSegment(sketch, "E22.top", {"start": v(-76.5, 16.5) * mm, "end": v(-83.5, 16.5) * mm});
            skLineSegment(sketch, "E22.left", {"start": v(-76.5, 18.5) * mm, "end": v(-76.5, 16.5) * mm});
            skLineSegment(sketch, "E22.right", {"start": v(-83.5, 18.5) * mm, "end": v(-83.5, 16.5) * mm});
            skPoint(sketch, "E22.middle", {"position": v(-80, 17.5) * mm});
            skCircle(sketch, "E23", {"center": v(-74, -20) * mm, "radius": 1 * mm});
            skLineSegment(sketch, "E24.bottom", {"start": v(-76.5, -18.5) * mm, "end": v(-83.5, -18.5) * mm});
            skLineSegment(sketch, "E24.top", {"start": v(-76.5, -16.63) * mm, "end": v(-83.5, -16.63) * mm});
            skLineSegment(sketch, "E24.left", {"start": v(-76.5, -18.5) * mm, "end": v(-76.5, -16.63) * mm});
            skLineSegment(sketch, "E24.right", {"start": v(-83.5, -18.5) * mm, "end": v(-83.5, -16.63) * mm});
            skPoint(sketch, "E24.middle", {"position": v(-80, -17.56) * mm});
            skLineSegment(sketch, "E25.bottom", {"start": v(-76.5, -21.5) * mm, "end": v(-83.5, -21.5) * mm});
            skLineSegment(sketch, "E25.top", {"start": v(-76.5, -23.67) * mm, "end": v(-83.5, -23.67) * mm});
            skLineSegment(sketch, "E25.left", {"start": v(-76.5, -21.5) * mm, "end": v(-76.5, -23.67) * mm});
            skLineSegment(sketch, "E25.right", {"start": v(-83.5, -21.5) * mm, "end": v(-83.5, -23.67) * mm});
            skPoint(sketch, "E25.middle", {"position": v(-80, -22.58) * mm});
            skCircle(sketch, "E26", {"center": v(-86, -20) * mm, "radius": 1 * mm});
            skSolve(sketch);
        }
        {
            var Q0;
            Q0=qSketchRegion(id+"F6",true);
            extrude(context, id + "F7", {"entities" : qUnion([Q0]), "operationType" : NewBodyOperationType.REMOVE, "oppositeDirection" : true, "depth" : 2 * mm});
        }
        {
            var Q0;
            Q0=makeQuery(id+"F1.opExtrude","CAP_FACE",FACE,{"disambiguationData":[OSD([sQuery(id+"F0.wireOp",EDGE,"E0.bottom"),sQuery(id+"F0.wireOp",EDGE,"E0.top"),sQuery(id+"F0.wireOp",EDGE,"E0.left"),sQuery(id+"F0.wireOp",EDGE,"E0.right")])],"isStart":false});
            var sketch = newSketch(context, id + "F8", { "sketchPlane" : qUnion([Q0])});
            skLineSegment(sketch, "E27.bottom", {"start": v(-70.25, 30) * mm, "end": v(-69.75, 30) * mm});
            skLineSegment(sketch, "E27.top", {"start": v(-70.25, -30) * mm, "end": v(-69.75, -30) * mm});
            skLineSegment(sketch, "E27.left", {"start": v(-70.25, 30) * mm, "end": v(-70.25, -30) * mm});
            skLineSegment(sketch, "E27.right", {"start": v(-69.75, 30) * mm, "end": v(-69.75, -30) * mm});
            skLineSegment(sketch, "E28.1.0.0", {"start": v(-50.25, 30) * mm, "end": v(-50.25, -30) * mm});
            skLineSegment(sketch, "E28.1.0.1", {"start": v(-49.75, 30) * mm, "end": v(-49.75, -30) * mm});
            skLineSegment(sketch, "E28.1.0.2", {"start": v(-50.25, -30) * mm, "end": v(-49.75, -30) * mm});
            skLineSegment(sketch, "E28.1.0.3", {"start": v(-50.25, 30) * mm, "end": v(-49.75, 30) * mm});
            skLineSegment(sketch, "E28.2.0.0", {"start": v(-30.25, 30) * mm, "end": v(-30.25, -30) * mm});
            skLineSegment(sketch, "E28.2.0.1", {"start": v(-29.75, 30) * mm, "end": v(-29.75, -30) * mm});
            skLineSegment(sketch, "E28.2.0.2", {"start": v(-30.25, -30) * mm, "end": v(-29.75, -30) * mm});
            skLineSegment(sketch, "E28.2.0.3", {"start": v(-30.25, 30) * mm, "end": v(-29.75, 30) * mm});
            skLineSegment(sketch, "E28.3.0.0", {"start": v(-10.25, 30) * mm, "end": v(-10.25, -30) * mm});
            skLineSegment(sketch, "E28.3.0.1", {"start": v(-9.75, 30) * mm, "end": v(-9.75, -30) * mm});
            skLineSegment(sketch, "E28.3.0.2", {"start": v(-10.25, -30) * mm, "end": v(-9.75, -30) * mm});
            skLineSegment(sketch, "E28.3.0.3", {"start": v(-10.25, 30) * mm, "end": v(-9.75, 30) * mm});
            skLineSegment(sketch, "E28.4.0.0", {"start": v(9.75, 30) * mm, "end": v(9.75, -30) * mm});
            skLineSegment(sketch, "E28.4.0.1", {"start": v(10.25, 30) * mm, "end": v(10.25, -30) * mm});
            skLineSegment(sketch, "E28.4.0.2", {"start": v(9.75, -30) * mm, "end": v(10.25, -30) * mm});
            skLineSegment(sketch, "E28.4.0.3", {"start": v(9.75, 30) * mm, "end": v(10.25, 30) * mm});
            skLineSegment(sketch, "E28.5.0.0", {"start": v(29.75, 30) * mm, "end": v(29.75, -30) * mm});
            skLineSegment(sketch, "E28.5.0.1", {"start": v(30.25, 30) * mm, "end": v(30.25, -30) * mm});
            skLineSegment(sketch, "E28.5.0.2", {"start": v(29.75, -30) * mm, "end": v(30.25, -30) * mm});
            skLineSegment(sketch, "E28.5.0.3", {"start": v(29.75, 30) * mm, "end": v(30.25, 30) * mm});
            skLineSegment(sketch, "E28.6.0.0", {"start": v(49.75, 30) * mm, "end": v(49.75, -30) * mm});
            skLineSegment(sketch, "E28.6.0.1", {"start": v(50.25, 30) * mm, "end": v(50.25, -30) * mm});
            skLineSegment(sketch, "E28.6.0.2", {"start": v(49.75, -30) * mm, "end": v(50.25, -30) * mm});
            skLineSegment(sketch, "E28.6.0.3", {"start": v(49.75, 30) * mm, "end": v(50.25, 30) * mm});
            skLineSegment(sketch, "E28.7.0.0", {"start": v(69.75, 30) * mm, "end": v(69.75, -30) * mm});
            skLineSegment(sketch, "E28.7.0.1", {"start": v(70.25, 30) * mm, "end": v(70.25, -30) * mm});
            skLineSegment(sketch, "E28.7.0.2", {"start": v(69.75, -30) * mm, "end": v(70.25, -30) * mm});
            skLineSegment(sketch, "E28.7.0.3", {"start": v(69.75, 30) * mm, "end": v(70.25, 30) * mm});
            skLineSegment(sketch, "E28.direction1", {"start": v(-70.25, -30) * mm, "end": v(-50.25, -30) * mm, "construction": true});
            skSolve(sketch);
        }
        {
            var Q0;
            Q0=qSketchRegion(id+"F8",true);
            extrude(context, id + "F9", {"entities" : qUnion([Q0]), "operationType" : NewBodyOperationType.ADD, "depth" : 1 * mm});
        }
    });
